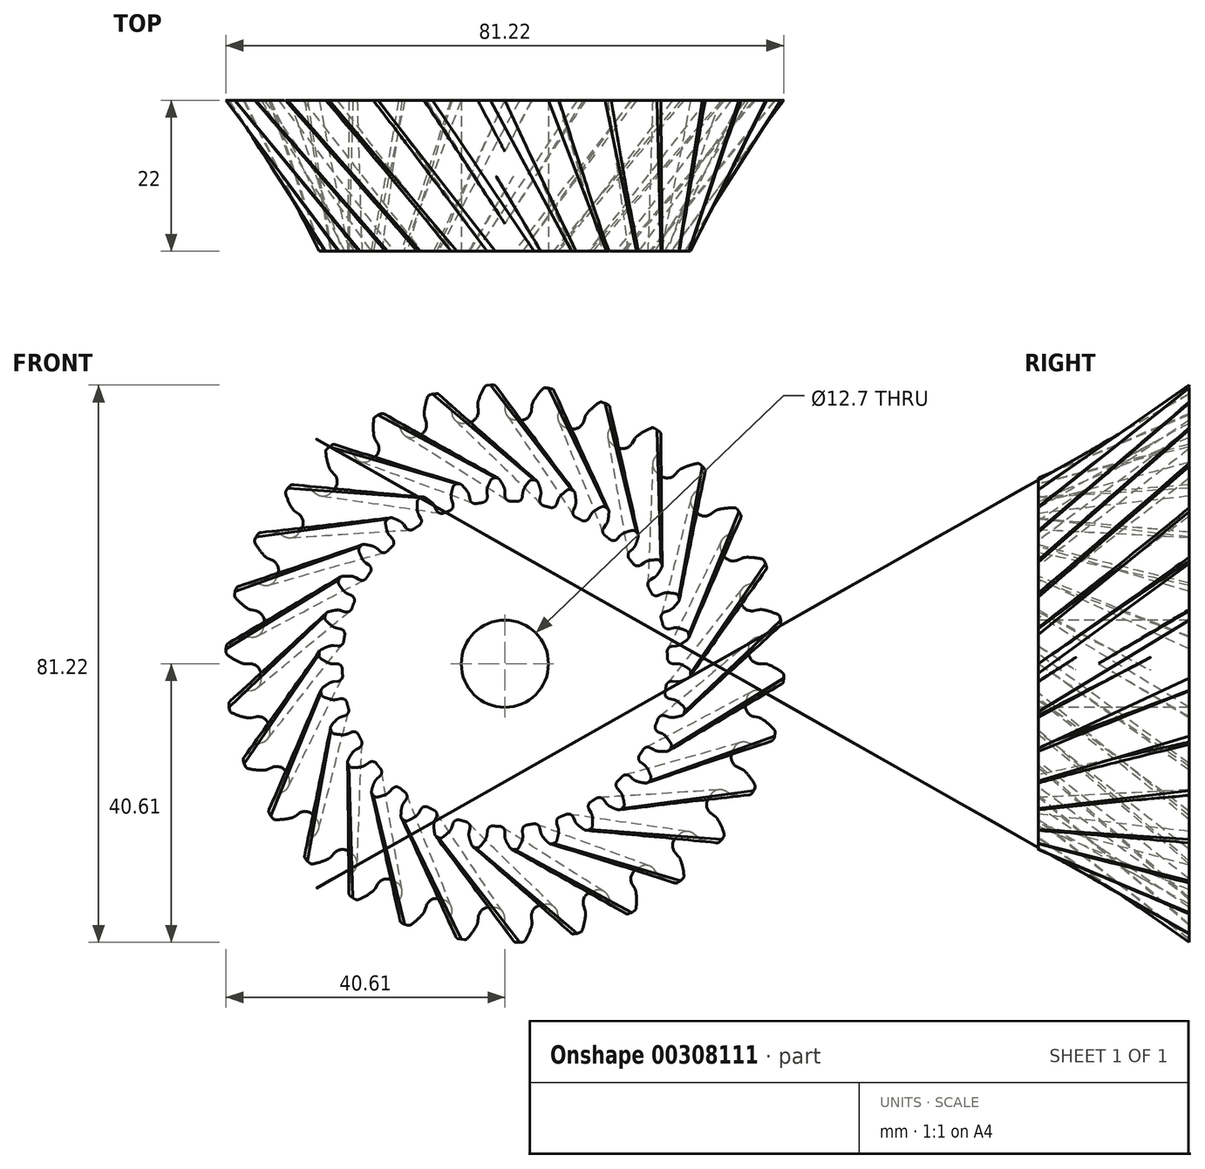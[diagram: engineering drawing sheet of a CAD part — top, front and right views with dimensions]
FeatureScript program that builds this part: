
annotation { "Feature Type Name" : "Feature", "Feature Type Description" : "" }
export const myFeature = defineFeature(function(context is Context, id is Id, definition is map)
    precondition{}
    {
        {
            var Q0;
            Q0=qCreatedBy(makeId("Front.planeOp"),FACE);
            var sketch = newSketch(context, id + "F0", { "sketchPlane" : qUnion([Q0])});
            skArc(sketch, "E0", {"start": v(-5.23, 35.17) * mm, "mid": v(-5.56, 35.12) * mm, "end": v(-5.9, 35.07) * mm});
            skArc(sketch, "E1.trimOffspring", {"start": v(-0.12, 38.41) * mm, "mid": v(-0.63, 39.45) * mm, "end": v(-1.27, 40.41) * mm});
            skLineSegment(sketch, "E2", {"start": v(-1.68, 40.61) * mm, "end": v(-2.13, 40.61) * mm});
            skLineSegment(sketch, "E3", {"start": v(0, 37.8) * mm, "end": v(0, 37.11) * mm});
            skLineSegment(sketch, "E4.MirrorCS", {"start": v(-2.58, 40.57) * mm, "end": v(-2.13, 40.61) * mm});
            skArc(sketch, "E5.MirrorCS", {"start": v(-3.9, 38.22) * mm, "mid": v(-3.5, 39.3) * mm, "end": v(-2.96, 40.32) * mm});
            skLineSegment(sketch, "E6.MirrorCS", {"start": v(-3.96, 37.58) * mm, "end": v(-3.89, 36.9) * mm});
            skPoint(sketch, "E7.visualSharp", {"position": v(-2.82, 40.54) * mm});
            skArc(sketch, "E7.filletArc", {"start": v(-2.58, 40.57) * mm, "mid": v(-2.8, 40.5) * mm, "end": v(-2.96, 40.32) * mm});
            skPoint(sketch, "E8.visualSharp", {"position": v(-1.43, 40.61) * mm});
            skArc(sketch, "E8.filletArc", {"start": v(-1.27, 40.41) * mm, "mid": v(-1.45, 40.56) * mm, "end": v(-1.68, 40.61) * mm});
            skPoint(sketch, "E9.visualSharp", {"position": v(-4, 37.9) * mm});
            skArc(sketch, "E9.filletArc", {"start": v(-3.9, 38.22) * mm, "mid": v(-3.96, 37.9) * mm, "end": v(-3.96, 37.58) * mm});
            skPoint(sketch, "E10.visualSharp", {"position": v(0, 38.1) * mm});
            skArc(sketch, "E10.filletArc", {"start": v(0, 37.8) * mm, "mid": v(-0.02, 38.1) * mm, "end": v(-0.12, 38.41) * mm});
            skPoint(sketch, "E11.visualSharp", {"position": v(0, 35.56) * mm});
            skArc(sketch, "E11.filletArc", {"start": v(0, 37.11) * mm, "mid": v(0.45, 36.02) * mm, "end": v(1.53, 35.53) * mm});
            skPoint(sketch, "E12.visualSharp", {"position": v(-3.73, 35.36) * mm});
            skArc(sketch, "E12.filletArc", {"start": v(-5.23, 35.17) * mm, "mid": v(-4.21, 35.77) * mm, "end": v(-3.89, 36.9) * mm});
            skArc(sketch, "E13.1.0", {"start": v(-12.43, 33.32) * mm, "mid": v(-11.56, 34.11) * mm, "end": v(-11.48, 35.3) * mm});
            skLineSegment(sketch, "E13.1.1", {"start": v(-11.69, 35.94) * mm, "end": v(-11.48, 35.3) * mm});
            skArc(sketch, "E13.1.2", {"start": v(-11.76, 36.57) * mm, "mid": v(-11.75, 36.25) * mm, "end": v(-11.69, 35.94) * mm});
            skArc(sketch, "E13.1.3", {"start": v(-11.76, 36.57) * mm, "mid": v(-11.59, 37.71) * mm, "end": v(-11.28, 38.83) * mm});
            skArc(sketch, "E13.1.4", {"start": v(-10.95, 39.15) * mm, "mid": v(-11.15, 39.02) * mm, "end": v(-11.28, 38.83) * mm});
            skLineSegment(sketch, "E13.1.5", {"start": v(-10.95, 39.15) * mm, "end": v(-10.53, 39.28) * mm});
            skLineSegment(sketch, "E13.1.6", {"start": v(-10.09, 39.38) * mm, "end": v(-10.53, 39.28) * mm});
            skArc(sketch, "E13.1.7", {"start": v(-9.65, 39.26) * mm, "mid": v(-9.85, 39.37) * mm, "end": v(-10.09, 39.38) * mm});
            skArc(sketch, "E13.1.8", {"start": v(-7.85, 36.97) * mm, "mid": v(-7.95, 37.27) * mm, "end": v(-8.1, 37.55) * mm});
            skLineSegment(sketch, "E13.1.9", {"start": v(-7.85, 36.97) * mm, "end": v(-7.7, 36.3) * mm});
            skArc(sketch, "E13.1.10", {"start": v(-7.7, 36.3) * mm, "mid": v(-7.05, 35.32) * mm, "end": v(-5.9, 35.07) * mm});
            skArc(sketch, "E13.1.11", {"start": v(-8.1, 37.55) * mm, "mid": v(-8.82, 38.45) * mm, "end": v(-9.65, 39.26) * mm});
            skArc(sketch, "E13.2.0", {"start": v(-19.09, 30) * mm, "mid": v(-18.4, 30.97) * mm, "end": v(-18.56, 32.14) * mm});
            skLineSegment(sketch, "E13.2.1", {"start": v(-18.9, 32.72) * mm, "end": v(-18.56, 32.14) * mm});
            skArc(sketch, "E13.2.2", {"start": v(-19.1, 33.33) * mm, "mid": v(-19.03, 33.01) * mm, "end": v(-18.9, 32.72) * mm});
            skArc(sketch, "E13.2.3", {"start": v(-19.1, 33.33) * mm, "mid": v(-19.17, 34.48) * mm, "end": v(-19.1, 35.63) * mm});
            skArc(sketch, "E13.2.4", {"start": v(-18.85, 36.01) * mm, "mid": v(-19.02, 35.85) * mm, "end": v(-19.1, 35.63) * mm});
            skLineSegment(sketch, "E13.2.5", {"start": v(-18.85, 36.01) * mm, "end": v(-18.46, 36.24) * mm});
            skLineSegment(sketch, "E13.2.6", {"start": v(-18.05, 36.42) * mm, "end": v(-18.46, 36.24) * mm});
            skArc(sketch, "E13.2.7", {"start": v(-17.6, 36.4) * mm, "mid": v(-17.82, 36.46) * mm, "end": v(-18.05, 36.42) * mm});
            skArc(sketch, "E13.2.8", {"start": v(-15.36, 34.53) * mm, "mid": v(-15.52, 34.8) * mm, "end": v(-15.73, 35.04) * mm});
            skLineSegment(sketch, "E13.2.9", {"start": v(-15.36, 34.53) * mm, "end": v(-15.09, 33.9) * mm});
            skArc(sketch, "E13.2.10", {"start": v(-15.09, 33.9) * mm, "mid": v(-14.24, 33.08) * mm, "end": v(-13.05, 33.08) * mm});
            skArc(sketch, "E13.2.11", {"start": v(-15.73, 35.04) * mm, "mid": v(-16.62, 35.78) * mm, "end": v(-17.6, 36.4) * mm});
            skArc(sketch, "E13.3.0", {"start": v(-24.9, 25.38) * mm, "mid": v(-24.43, 26.46) * mm, "end": v(-24.84, 27.57) * mm});
            skLineSegment(sketch, "E13.3.1", {"start": v(-25.3, 28.08) * mm, "end": v(-24.84, 27.57) * mm});
            skArc(sketch, "E13.3.2", {"start": v(-25.62, 28.63) * mm, "mid": v(-25.48, 28.34) * mm, "end": v(-25.3, 28.08) * mm});
            skArc(sketch, "E13.3.3", {"start": v(-25.62, 28.63) * mm, "mid": v(-25.92, 29.74) * mm, "end": v(-26.1, 30.88) * mm});
            skArc(sketch, "E13.3.4", {"start": v(-25.93, 31.3) * mm, "mid": v(-26.06, 31.11) * mm, "end": v(-26.1, 30.88) * mm});
            skLineSegment(sketch, "E13.3.5", {"start": v(-25.93, 31.3) * mm, "end": v(-25.6, 31.6) * mm});
            skLineSegment(sketch, "E13.3.6", {"start": v(-25.23, 31.87) * mm, "end": v(-25.6, 31.6) * mm});
            skArc(sketch, "E13.3.7", {"start": v(-24.78, 31.95) * mm, "mid": v(-25.02, 31.96) * mm, "end": v(-25.23, 31.87) * mm});
            skArc(sketch, "E13.3.8", {"start": v(-22.2, 30.58) * mm, "mid": v(-22.42, 30.82) * mm, "end": v(-22.67, 31) * mm});
            skLineSegment(sketch, "E13.3.9", {"start": v(-22.2, 30.58) * mm, "end": v(-21.8, 30.03) * mm});
            skArc(sketch, "E13.3.10", {"start": v(-21.8, 30.03) * mm, "mid": v(-20.8, 29.4) * mm, "end": v(-19.65, 29.64) * mm});
            skArc(sketch, "E13.3.11", {"start": v(-22.67, 31) * mm, "mid": v(-23.7, 31.54) * mm, "end": v(-24.78, 31.95) * mm});
            skArc(sketch, "E13.4.0", {"start": v(-29.64, 19.65) * mm, "mid": v(-29.4, 20.8) * mm, "end": v(-30.03, 21.8) * mm});
            skLineSegment(sketch, "E13.4.1", {"start": v(-30.58, 22.2) * mm, "end": v(-30.03, 21.8) * mm});
            skArc(sketch, "E13.4.2", {"start": v(-31, 22.67) * mm, "mid": v(-30.82, 22.42) * mm, "end": v(-30.58, 22.2) * mm});
            skArc(sketch, "E13.4.3", {"start": v(-31, 22.67) * mm, "mid": v(-31.54, 23.7) * mm, "end": v(-31.95, 24.78) * mm});
            skArc(sketch, "E13.4.4", {"start": v(-31.87, 25.23) * mm, "mid": v(-31.96, 25.02) * mm, "end": v(-31.95, 24.78) * mm});
            skLineSegment(sketch, "E13.4.5", {"start": v(-31.87, 25.23) * mm, "end": v(-31.6, 25.6) * mm});
            skLineSegment(sketch, "E13.4.6", {"start": v(-31.3, 25.93) * mm, "end": v(-31.6, 25.6) * mm});
            skArc(sketch, "E13.4.7", {"start": v(-30.88, 26.1) * mm, "mid": v(-31.11, 26.06) * mm, "end": v(-31.3, 25.93) * mm});
            skArc(sketch, "E13.4.8", {"start": v(-28.08, 25.3) * mm, "mid": v(-28.34, 25.48) * mm, "end": v(-28.63, 25.62) * mm});
            skLineSegment(sketch, "E13.4.9", {"start": v(-28.08, 25.3) * mm, "end": v(-27.57, 24.84) * mm});
            skArc(sketch, "E13.4.10", {"start": v(-27.57, 24.84) * mm, "mid": v(-26.46, 24.43) * mm, "end": v(-25.38, 24.9) * mm});
            skArc(sketch, "E13.4.11", {"start": v(-28.63, 25.62) * mm, "mid": v(-29.74, 25.92) * mm, "end": v(-30.88, 26.1) * mm});
            skArc(sketch, "E13.5.0", {"start": v(-33.08, 13.05) * mm, "mid": v(-33.08, 14.24) * mm, "end": v(-33.9, 15.09) * mm});
            skLineSegment(sketch, "E13.5.1", {"start": v(-34.53, 15.36) * mm, "end": v(-33.9, 15.09) * mm});
            skArc(sketch, "E13.5.2", {"start": v(-35.04, 15.73) * mm, "mid": v(-34.8, 15.52) * mm, "end": v(-34.53, 15.36) * mm});
            skArc(sketch, "E13.5.3", {"start": v(-35.04, 15.73) * mm, "mid": v(-35.78, 16.62) * mm, "end": v(-36.4, 17.6) * mm});
            skArc(sketch, "E13.5.4", {"start": v(-36.42, 18.05) * mm, "mid": v(-36.46, 17.82) * mm, "end": v(-36.4, 17.6) * mm});
            skLineSegment(sketch, "E13.5.5", {"start": v(-36.42, 18.05) * mm, "end": v(-36.24, 18.46) * mm});
            skLineSegment(sketch, "E13.5.6", {"start": v(-36.01, 18.85) * mm, "end": v(-36.24, 18.46) * mm});
            skArc(sketch, "E13.5.7", {"start": v(-35.63, 19.1) * mm, "mid": v(-35.85, 19.02) * mm, "end": v(-36.01, 18.85) * mm});
            skArc(sketch, "E13.5.8", {"start": v(-32.72, 18.9) * mm, "mid": v(-33.01, 19.03) * mm, "end": v(-33.33, 19.1) * mm});
            skLineSegment(sketch, "E13.5.9", {"start": v(-32.72, 18.9) * mm, "end": v(-32.14, 18.56) * mm});
            skArc(sketch, "E13.5.10", {"start": v(-32.14, 18.56) * mm, "mid": v(-30.97, 18.4) * mm, "end": v(-30, 19.09) * mm});
            skArc(sketch, "E13.5.11", {"start": v(-33.33, 19.1) * mm, "mid": v(-34.48, 19.17) * mm, "end": v(-35.63, 19.1) * mm});
            skArc(sketch, "E13.6.0", {"start": v(-35.07, 5.9) * mm, "mid": v(-35.32, 7.05) * mm, "end": v(-36.3, 7.7) * mm});
            skLineSegment(sketch, "E13.6.1", {"start": v(-36.97, 7.85) * mm, "end": v(-36.3, 7.7) * mm});
            skArc(sketch, "E13.6.2", {"start": v(-37.55, 8.1) * mm, "mid": v(-37.27, 7.95) * mm, "end": v(-36.97, 7.85) * mm});
            skArc(sketch, "E13.6.3", {"start": v(-37.55, 8.1) * mm, "mid": v(-38.45, 8.82) * mm, "end": v(-39.26, 9.65) * mm});
            skArc(sketch, "E13.6.4", {"start": v(-39.38, 10.09) * mm, "mid": v(-39.37, 9.85) * mm, "end": v(-39.26, 9.65) * mm});
            skLineSegment(sketch, "E13.6.5", {"start": v(-39.38, 10.09) * mm, "end": v(-39.28, 10.53) * mm});
            skLineSegment(sketch, "E13.6.6", {"start": v(-39.15, 10.95) * mm, "end": v(-39.28, 10.53) * mm});
            skArc(sketch, "E13.6.7", {"start": v(-38.83, 11.28) * mm, "mid": v(-39.02, 11.15) * mm, "end": v(-39.15, 10.95) * mm});
            skArc(sketch, "E13.6.8", {"start": v(-35.94, 11.69) * mm, "mid": v(-36.25, 11.75) * mm, "end": v(-36.57, 11.76) * mm});
            skLineSegment(sketch, "E13.6.9", {"start": v(-35.94, 11.69) * mm, "end": v(-35.3, 11.48) * mm});
            skArc(sketch, "E13.6.10", {"start": v(-35.3, 11.48) * mm, "mid": v(-34.11, 11.56) * mm, "end": v(-33.32, 12.43) * mm});
            skArc(sketch, "E13.6.11", {"start": v(-36.57, 11.76) * mm, "mid": v(-37.71, 11.59) * mm, "end": v(-38.83, 11.28) * mm});
            skArc(sketch, "E13.7.0", {"start": v(-35.53, -1.53) * mm, "mid": v(-36.02, -0.45) * mm, "end": v(-37.11, 0) * mm});
            skLineSegment(sketch, "E13.7.1", {"start": v(-37.8, 0) * mm, "end": v(-37.11, 0) * mm});
            skArc(sketch, "E13.7.2", {"start": v(-38.41, 0.12) * mm, "mid": v(-38.1, 0.02) * mm, "end": v(-37.8, 0) * mm});
            skArc(sketch, "E13.7.3", {"start": v(-38.41, 0.12) * mm, "mid": v(-39.45, 0.63) * mm, "end": v(-40.41, 1.27) * mm});
            skArc(sketch, "E13.7.4", {"start": v(-40.61, 1.68) * mm, "mid": v(-40.56, 1.45) * mm, "end": v(-40.41, 1.27) * mm});
            skLineSegment(sketch, "E13.7.5", {"start": v(-40.61, 1.68) * mm, "end": v(-40.61, 2.13) * mm});
            skLineSegment(sketch, "E13.7.6", {"start": v(-40.57, 2.58) * mm, "end": v(-40.61, 2.13) * mm});
            skArc(sketch, "E13.7.7", {"start": v(-40.32, 2.96) * mm, "mid": v(-40.5, 2.8) * mm, "end": v(-40.57, 2.58) * mm});
            skArc(sketch, "E13.7.8", {"start": v(-37.58, 3.96) * mm, "mid": v(-37.9, 3.96) * mm, "end": v(-38.22, 3.9) * mm});
            skLineSegment(sketch, "E13.7.9", {"start": v(-37.58, 3.96) * mm, "end": v(-36.9, 3.89) * mm});
            skArc(sketch, "E13.7.10", {"start": v(-36.9, 3.89) * mm, "mid": v(-35.77, 4.21) * mm, "end": v(-35.17, 5.23) * mm});
            skArc(sketch, "E13.7.11", {"start": v(-38.22, 3.9) * mm, "mid": v(-39.3, 3.5) * mm, "end": v(-40.32, 2.96) * mm});
            skArc(sketch, "E13.8.0", {"start": v(-34.43, -8.88) * mm, "mid": v(-35.13, -7.93) * mm, "end": v(-36.3, -7.72) * mm});
            skLineSegment(sketch, "E13.8.1", {"start": v(-36.96, -7.87) * mm, "end": v(-36.3, -7.72) * mm});
            skArc(sketch, "E13.8.2", {"start": v(-37.6, -7.87) * mm, "mid": v(-37.28, -7.9) * mm, "end": v(-36.96, -7.87) * mm});
            skArc(sketch, "E13.8.3", {"start": v(-37.6, -7.87) * mm, "mid": v(-38.72, -7.58) * mm, "end": v(-39.8, -7.16) * mm});
            skArc(sketch, "E13.8.4", {"start": v(-40.08, -6.8) * mm, "mid": v(-39.98, -7.01) * mm, "end": v(-39.8, -7.16) * mm});
            skLineSegment(sketch, "E13.8.5", {"start": v(-40.08, -6.8) * mm, "end": v(-40.17, -6.36) * mm});
            skLineSegment(sketch, "E13.8.6", {"start": v(-40.22, -5.92) * mm, "end": v(-40.17, -6.36) * mm});
            skArc(sketch, "E13.8.7", {"start": v(-40.06, -5.5) * mm, "mid": v(-40.19, -5.68) * mm, "end": v(-40.22, -5.92) * mm});
            skArc(sketch, "E13.8.8", {"start": v(-37.59, -3.94) * mm, "mid": v(-37.9, -4) * mm, "end": v(-38.2, -4.13) * mm});
            skLineSegment(sketch, "E13.8.9", {"start": v(-37.59, -3.94) * mm, "end": v(-36.91, -3.87) * mm});
            skArc(sketch, "E13.8.10", {"start": v(-36.91, -3.87) * mm, "mid": v(-35.86, -3.32) * mm, "end": v(-35.5, -2.2) * mm});
            skArc(sketch, "E13.8.11", {"start": v(-38.2, -4.13) * mm, "mid": v(-39.17, -4.75) * mm, "end": v(-40.06, -5.5) * mm});
            skArc(sketch, "E13.9.0", {"start": v(-31.83, -15.85) * mm, "mid": v(-32.72, -15.06) * mm, "end": v(-33.9, -15.1) * mm});
            skLineSegment(sketch, "E13.9.1", {"start": v(-34.52, -15.38) * mm, "end": v(-33.9, -15.1) * mm});
            skArc(sketch, "E13.9.2", {"start": v(-35.14, -15.52) * mm, "mid": v(-34.82, -15.48) * mm, "end": v(-34.52, -15.38) * mm});
            skArc(sketch, "E13.9.3", {"start": v(-35.14, -15.52) * mm, "mid": v(-36.3, -15.46) * mm, "end": v(-37.44, -15.27) * mm});
            skArc(sketch, "E13.9.4", {"start": v(-37.79, -14.99) * mm, "mid": v(-37.65, -15.17) * mm, "end": v(-37.44, -15.27) * mm});
            skLineSegment(sketch, "E13.9.5", {"start": v(-37.79, -14.99) * mm, "end": v(-37.97, -14.58) * mm});
            skLineSegment(sketch, "E13.9.6", {"start": v(-38.1, -14.15) * mm, "end": v(-37.97, -14.58) * mm});
            skArc(sketch, "E13.9.7", {"start": v(-38.04, -13.7) * mm, "mid": v(-38.13, -13.92) * mm, "end": v(-38.1, -14.15) * mm});
            skArc(sketch, "E13.9.8", {"start": v(-35.94, -11.67) * mm, "mid": v(-36.24, -11.8) * mm, "end": v(-36.5, -11.98) * mm});
            skLineSegment(sketch, "E13.9.9", {"start": v(-35.94, -11.67) * mm, "end": v(-35.3, -11.46) * mm});
            skArc(sketch, "E13.9.10", {"start": v(-35.3, -11.46) * mm, "mid": v(-34.4, -10.7) * mm, "end": v(-34.26, -9.53) * mm});
            skArc(sketch, "E13.9.11", {"start": v(-36.5, -11.98) * mm, "mid": v(-37.32, -12.8) * mm, "end": v(-38.04, -13.7) * mm});
            skArc(sketch, "E13.10.0", {"start": v(-27.84, -22.12) * mm, "mid": v(-28.87, -21.53) * mm, "end": v(-30.02, -21.82) * mm});
            skLineSegment(sketch, "E13.10.1", {"start": v(-30.57, -22.22) * mm, "end": v(-30.02, -21.82) * mm});
            skArc(sketch, "E13.10.2", {"start": v(-31.15, -22.48) * mm, "mid": v(-30.84, -22.38) * mm, "end": v(-30.57, -22.22) * mm});
            skArc(sketch, "E13.10.3", {"start": v(-31.15, -22.48) * mm, "mid": v(-32.29, -22.67) * mm, "end": v(-33.44, -22.72) * mm});
            skArc(sketch, "E13.10.4", {"start": v(-33.85, -22.51) * mm, "mid": v(-33.67, -22.67) * mm, "end": v(-33.44, -22.72) * mm});
            skLineSegment(sketch, "E13.10.5", {"start": v(-33.85, -22.51) * mm, "end": v(-34.1, -22.15) * mm});
            skLineSegment(sketch, "E13.10.6", {"start": v(-34.33, -21.76) * mm, "end": v(-34.1, -22.15) * mm});
            skArc(sketch, "E13.10.7", {"start": v(-34.36, -21.3) * mm, "mid": v(-34.4, -21.54) * mm, "end": v(-34.33, -21.76) * mm});
            skArc(sketch, "E13.10.8", {"start": v(-32.73, -18.89) * mm, "mid": v(-33, -19.07) * mm, "end": v(-33.2, -19.3) * mm});
            skLineSegment(sketch, "E13.10.9", {"start": v(-32.73, -18.89) * mm, "end": v(-32.15, -18.55) * mm});
            skArc(sketch, "E13.10.10", {"start": v(-32.15, -18.55) * mm, "mid": v(-31.41, -17.62) * mm, "end": v(-31.53, -16.44) * mm});
            skArc(sketch, "E13.10.11", {"start": v(-33.2, -19.3) * mm, "mid": v(-33.85, -20.27) * mm, "end": v(-34.36, -21.3) * mm});
            skArc(sketch, "E13.11.0", {"start": v(-22.64, -27.42) * mm, "mid": v(-23.76, -27.07) * mm, "end": v(-24.83, -27.59) * mm});
            skLineSegment(sketch, "E13.11.1", {"start": v(-25.28, -28.1) * mm, "end": v(-24.83, -27.59) * mm});
            skArc(sketch, "E13.11.2", {"start": v(-25.8, -28.47) * mm, "mid": v(-25.52, -28.3) * mm, "end": v(-25.28, -28.1) * mm});
            skArc(sketch, "E13.11.3", {"start": v(-25.8, -28.47) * mm, "mid": v(-26.87, -28.9) * mm, "end": v(-27.99, -29.18) * mm});
            skArc(sketch, "E13.11.4", {"start": v(-28.42, -29.06) * mm, "mid": v(-28.22, -29.17) * mm, "end": v(-27.99, -29.18) * mm});
            skLineSegment(sketch, "E13.11.5", {"start": v(-28.42, -29.06) * mm, "end": v(-28.76, -28.76) * mm});
            skLineSegment(sketch, "E13.11.6", {"start": v(-29.06, -28.42) * mm, "end": v(-28.76, -28.76) * mm});
            skArc(sketch, "E13.11.7", {"start": v(-29.18, -27.99) * mm, "mid": v(-29.17, -28.22) * mm, "end": v(-29.06, -28.42) * mm});
            skArc(sketch, "E13.11.8", {"start": v(-28.1, -25.28) * mm, "mid": v(-28.3, -25.52) * mm, "end": v(-28.47, -25.8) * mm});
            skLineSegment(sketch, "E13.11.9", {"start": v(-28.1, -25.28) * mm, "end": v(-27.59, -24.83) * mm});
            skArc(sketch, "E13.11.10", {"start": v(-27.59, -24.83) * mm, "mid": v(-27.07, -23.76) * mm, "end": v(-27.42, -22.64) * mm});
            skArc(sketch, "E13.11.11", {"start": v(-28.47, -25.8) * mm, "mid": v(-28.9, -26.87) * mm, "end": v(-29.18, -27.99) * mm});
            skArc(sketch, "E13.12.0", {"start": v(-16.44, -31.53) * mm, "mid": v(-17.62, -31.41) * mm, "end": v(-18.55, -32.15) * mm});
            skLineSegment(sketch, "E13.12.1", {"start": v(-18.89, -32.73) * mm, "end": v(-18.55, -32.15) * mm});
            skArc(sketch, "E13.12.2", {"start": v(-19.3, -33.2) * mm, "mid": v(-19.07, -33) * mm, "end": v(-18.89, -32.73) * mm});
            skArc(sketch, "E13.12.3", {"start": v(-19.3, -33.2) * mm, "mid": v(-20.27, -33.85) * mm, "end": v(-21.3, -34.36) * mm});
            skArc(sketch, "E13.12.4", {"start": v(-21.76, -34.33) * mm, "mid": v(-21.54, -34.4) * mm, "end": v(-21.3, -34.36) * mm});
            skLineSegment(sketch, "E13.12.5", {"start": v(-21.76, -34.33) * mm, "end": v(-22.15, -34.1) * mm});
            skLineSegment(sketch, "E13.12.6", {"start": v(-22.51, -33.85) * mm, "end": v(-22.15, -34.1) * mm});
            skArc(sketch, "E13.12.7", {"start": v(-22.72, -33.44) * mm, "mid": v(-22.67, -33.67) * mm, "end": v(-22.51, -33.85) * mm});
            skArc(sketch, "E13.12.8", {"start": v(-22.22, -30.57) * mm, "mid": v(-22.38, -30.84) * mm, "end": v(-22.48, -31.15) * mm});
            skLineSegment(sketch, "E13.12.9", {"start": v(-22.22, -30.57) * mm, "end": v(-21.82, -30.02) * mm});
            skArc(sketch, "E13.12.10", {"start": v(-21.82, -30.02) * mm, "mid": v(-21.53, -28.87) * mm, "end": v(-22.12, -27.84) * mm});
            skArc(sketch, "E13.12.11", {"start": v(-22.48, -31.15) * mm, "mid": v(-22.67, -32.29) * mm, "end": v(-22.72, -33.44) * mm});
            skArc(sketch, "E13.13.0", {"start": v(-9.53, -34.26) * mm, "mid": v(-10.7, -34.4) * mm, "end": v(-11.46, -35.3) * mm});
            skLineSegment(sketch, "E13.13.1", {"start": v(-11.67, -35.94) * mm, "end": v(-11.46, -35.3) * mm});
            skArc(sketch, "E13.13.2", {"start": v(-11.98, -36.5) * mm, "mid": v(-11.8, -36.24) * mm, "end": v(-11.67, -35.94) * mm});
            skArc(sketch, "E13.13.3", {"start": v(-11.98, -36.5) * mm, "mid": v(-12.8, -37.32) * mm, "end": v(-13.7, -38.04) * mm});
            skArc(sketch, "E13.13.4", {"start": v(-14.15, -38.1) * mm, "mid": v(-13.92, -38.13) * mm, "end": v(-13.7, -38.04) * mm});
            skLineSegment(sketch, "E13.13.5", {"start": v(-14.15, -38.1) * mm, "end": v(-14.58, -37.97) * mm});
            skLineSegment(sketch, "E13.13.6", {"start": v(-14.99, -37.79) * mm, "end": v(-14.58, -37.97) * mm});
            skArc(sketch, "E13.13.7", {"start": v(-15.27, -37.44) * mm, "mid": v(-15.17, -37.65) * mm, "end": v(-14.99, -37.79) * mm});
            skArc(sketch, "E13.13.8", {"start": v(-15.38, -34.52) * mm, "mid": v(-15.48, -34.82) * mm, "end": v(-15.52, -35.14) * mm});
            skLineSegment(sketch, "E13.13.9", {"start": v(-15.38, -34.52) * mm, "end": v(-15.1, -33.9) * mm});
            skArc(sketch, "E13.13.10", {"start": v(-15.1, -33.9) * mm, "mid": v(-15.06, -32.72) * mm, "end": v(-15.85, -31.83) * mm});
            skArc(sketch, "E13.13.11", {"start": v(-15.52, -35.14) * mm, "mid": v(-15.46, -36.3) * mm, "end": v(-15.27, -37.44) * mm});
            skArc(sketch, "E13.14.0", {"start": v(-2.2, -35.5) * mm, "mid": v(-3.32, -35.86) * mm, "end": v(-3.87, -36.91) * mm});
            skLineSegment(sketch, "E13.14.1", {"start": v(-3.94, -37.59) * mm, "end": v(-3.87, -36.91) * mm});
            skArc(sketch, "E13.14.2", {"start": v(-4.13, -38.2) * mm, "mid": v(-4, -37.9) * mm, "end": v(-3.94, -37.59) * mm});
            skArc(sketch, "E13.14.3", {"start": v(-4.13, -38.2) * mm, "mid": v(-4.75, -39.17) * mm, "end": v(-5.5, -40.06) * mm});
            skArc(sketch, "E13.14.4", {"start": v(-5.92, -40.22) * mm, "mid": v(-5.68, -40.19) * mm, "end": v(-5.5, -40.06) * mm});
            skLineSegment(sketch, "E13.14.5", {"start": v(-5.92, -40.22) * mm, "end": v(-6.36, -40.17) * mm});
            skLineSegment(sketch, "E13.14.6", {"start": v(-6.8, -40.08) * mm, "end": v(-6.36, -40.17) * mm});
            skArc(sketch, "E13.14.7", {"start": v(-7.16, -39.8) * mm, "mid": v(-7.01, -39.98) * mm, "end": v(-6.8, -40.08) * mm});
            skArc(sketch, "E13.14.8", {"start": v(-7.87, -36.96) * mm, "mid": v(-7.9, -37.28) * mm, "end": v(-7.87, -37.6) * mm});
            skLineSegment(sketch, "E13.14.9", {"start": v(-7.87, -36.96) * mm, "end": v(-7.72, -36.3) * mm});
            skArc(sketch, "E13.14.10", {"start": v(-7.72, -36.3) * mm, "mid": v(-7.93, -35.13) * mm, "end": v(-8.88, -34.43) * mm});
            skArc(sketch, "E13.14.11", {"start": v(-7.87, -37.6) * mm, "mid": v(-7.58, -38.72) * mm, "end": v(-7.16, -39.8) * mm});
            skArc(sketch, "E13.15.0", {"start": v(5.23, -35.17) * mm, "mid": v(4.21, -35.77) * mm, "end": v(3.89, -36.9) * mm});
            skLineSegment(sketch, "E13.15.1", {"start": v(3.96, -37.58) * mm, "end": v(3.89, -36.9) * mm});
            skArc(sketch, "E13.15.2", {"start": v(3.9, -38.22) * mm, "mid": v(3.96, -37.9) * mm, "end": v(3.96, -37.58) * mm});
            skArc(sketch, "E13.15.3", {"start": v(3.9, -38.22) * mm, "mid": v(3.5, -39.3) * mm, "end": v(2.96, -40.32) * mm});
            skArc(sketch, "E13.15.4", {"start": v(2.58, -40.57) * mm, "mid": v(2.8, -40.5) * mm, "end": v(2.96, -40.32) * mm});
            skLineSegment(sketch, "E13.15.5", {"start": v(2.58, -40.57) * mm, "end": v(2.13, -40.61) * mm});
            skLineSegment(sketch, "E13.15.6", {"start": v(1.68, -40.61) * mm, "end": v(2.13, -40.61) * mm});
            skArc(sketch, "E13.15.7", {"start": v(1.27, -40.41) * mm, "mid": v(1.45, -40.56) * mm, "end": v(1.68, -40.61) * mm});
            skArc(sketch, "E13.15.8", {"start": v(0, -37.8) * mm, "mid": v(0.02, -38.1) * mm, "end": v(0.12, -38.41) * mm});
            skLineSegment(sketch, "E13.15.9", {"start": v(0, -37.8) * mm, "end": v(0, -37.11) * mm});
            skArc(sketch, "E13.15.10", {"start": v(0, -37.11) * mm, "mid": v(-0.45, -36.02) * mm, "end": v(-1.53, -35.53) * mm});
            skArc(sketch, "E13.15.11", {"start": v(0.12, -38.41) * mm, "mid": v(0.63, -39.45) * mm, "end": v(1.27, -40.41) * mm});
            skArc(sketch, "E13.16.0", {"start": v(12.43, -33.32) * mm, "mid": v(11.56, -34.11) * mm, "end": v(11.48, -35.3) * mm});
            skLineSegment(sketch, "E13.16.1", {"start": v(11.69, -35.94) * mm, "end": v(11.48, -35.3) * mm});
            skArc(sketch, "E13.16.2", {"start": v(11.76, -36.57) * mm, "mid": v(11.75, -36.25) * mm, "end": v(11.69, -35.94) * mm});
            skArc(sketch, "E13.16.3", {"start": v(11.76, -36.57) * mm, "mid": v(11.59, -37.71) * mm, "end": v(11.28, -38.83) * mm});
            skArc(sketch, "E13.16.4", {"start": v(10.95, -39.15) * mm, "mid": v(11.15, -39.02) * mm, "end": v(11.28, -38.83) * mm});
            skLineSegment(sketch, "E13.16.5", {"start": v(10.95, -39.15) * mm, "end": v(10.53, -39.28) * mm});
            skLineSegment(sketch, "E13.16.6", {"start": v(10.09, -39.38) * mm, "end": v(10.53, -39.28) * mm});
            skArc(sketch, "E13.16.7", {"start": v(9.65, -39.26) * mm, "mid": v(9.85, -39.37) * mm, "end": v(10.09, -39.38) * mm});
            skArc(sketch, "E13.16.8", {"start": v(7.85, -36.97) * mm, "mid": v(7.95, -37.27) * mm, "end": v(8.1, -37.55) * mm});
            skLineSegment(sketch, "E13.16.9", {"start": v(7.85, -36.97) * mm, "end": v(7.7, -36.3) * mm});
            skArc(sketch, "E13.16.10", {"start": v(7.7, -36.3) * mm, "mid": v(7.05, -35.32) * mm, "end": v(5.9, -35.07) * mm});
            skArc(sketch, "E13.16.11", {"start": v(8.1, -37.55) * mm, "mid": v(8.82, -38.45) * mm, "end": v(9.65, -39.26) * mm});
            skArc(sketch, "E13.17.0", {"start": v(19.09, -30) * mm, "mid": v(18.4, -30.97) * mm, "end": v(18.56, -32.14) * mm});
            skLineSegment(sketch, "E13.17.1", {"start": v(18.9, -32.72) * mm, "end": v(18.56, -32.14) * mm});
            skArc(sketch, "E13.17.2", {"start": v(19.1, -33.33) * mm, "mid": v(19.03, -33.01) * mm, "end": v(18.9, -32.72) * mm});
            skArc(sketch, "E13.17.3", {"start": v(19.1, -33.33) * mm, "mid": v(19.17, -34.48) * mm, "end": v(19.1, -35.63) * mm});
            skArc(sketch, "E13.17.4", {"start": v(18.85, -36.01) * mm, "mid": v(19.02, -35.85) * mm, "end": v(19.1, -35.63) * mm});
            skLineSegment(sketch, "E13.17.5", {"start": v(18.85, -36.01) * mm, "end": v(18.46, -36.24) * mm});
            skLineSegment(sketch, "E13.17.6", {"start": v(18.05, -36.42) * mm, "end": v(18.46, -36.24) * mm});
            skArc(sketch, "E13.17.7", {"start": v(17.6, -36.4) * mm, "mid": v(17.82, -36.46) * mm, "end": v(18.05, -36.42) * mm});
            skArc(sketch, "E13.17.8", {"start": v(15.36, -34.53) * mm, "mid": v(15.52, -34.8) * mm, "end": v(15.73, -35.04) * mm});
            skLineSegment(sketch, "E13.17.9", {"start": v(15.36, -34.53) * mm, "end": v(15.09, -33.9) * mm});
            skArc(sketch, "E13.17.10", {"start": v(15.09, -33.9) * mm, "mid": v(14.24, -33.08) * mm, "end": v(13.05, -33.08) * mm});
            skArc(sketch, "E13.17.11", {"start": v(15.73, -35.04) * mm, "mid": v(16.62, -35.78) * mm, "end": v(17.6, -36.4) * mm});
            skArc(sketch, "E13.18.0", {"start": v(24.9, -25.38) * mm, "mid": v(24.43, -26.46) * mm, "end": v(24.84, -27.57) * mm});
            skLineSegment(sketch, "E13.18.1", {"start": v(25.3, -28.08) * mm, "end": v(24.84, -27.57) * mm});
            skArc(sketch, "E13.18.2", {"start": v(25.62, -28.63) * mm, "mid": v(25.48, -28.34) * mm, "end": v(25.3, -28.08) * mm});
            skArc(sketch, "E13.18.3", {"start": v(25.62, -28.63) * mm, "mid": v(25.92, -29.74) * mm, "end": v(26.1, -30.88) * mm});
            skArc(sketch, "E13.18.4", {"start": v(25.93, -31.3) * mm, "mid": v(26.06, -31.11) * mm, "end": v(26.1, -30.88) * mm});
            skLineSegment(sketch, "E13.18.5", {"start": v(25.93, -31.3) * mm, "end": v(25.6, -31.6) * mm});
            skLineSegment(sketch, "E13.18.6", {"start": v(25.23, -31.87) * mm, "end": v(25.6, -31.6) * mm});
            skArc(sketch, "E13.18.7", {"start": v(24.78, -31.95) * mm, "mid": v(25.02, -31.96) * mm, "end": v(25.23, -31.87) * mm});
            skArc(sketch, "E13.18.8", {"start": v(22.2, -30.58) * mm, "mid": v(22.42, -30.82) * mm, "end": v(22.67, -31) * mm});
            skLineSegment(sketch, "E13.18.9", {"start": v(22.2, -30.58) * mm, "end": v(21.8, -30.03) * mm});
            skArc(sketch, "E13.18.10", {"start": v(21.8, -30.03) * mm, "mid": v(20.8, -29.4) * mm, "end": v(19.65, -29.64) * mm});
            skArc(sketch, "E13.18.11", {"start": v(22.67, -31) * mm, "mid": v(23.7, -31.54) * mm, "end": v(24.78, -31.95) * mm});
            skArc(sketch, "E13.19.0", {"start": v(29.64, -19.65) * mm, "mid": v(29.4, -20.8) * mm, "end": v(30.03, -21.8) * mm});
            skLineSegment(sketch, "E13.19.1", {"start": v(30.58, -22.2) * mm, "end": v(30.03, -21.8) * mm});
            skArc(sketch, "E13.19.2", {"start": v(31, -22.67) * mm, "mid": v(30.82, -22.42) * mm, "end": v(30.58, -22.2) * mm});
            skArc(sketch, "E13.19.3", {"start": v(31, -22.67) * mm, "mid": v(31.54, -23.7) * mm, "end": v(31.95, -24.78) * mm});
            skArc(sketch, "E13.19.4", {"start": v(31.87, -25.23) * mm, "mid": v(31.96, -25.02) * mm, "end": v(31.95, -24.78) * mm});
            skLineSegment(sketch, "E13.19.5", {"start": v(31.87, -25.23) * mm, "end": v(31.6, -25.6) * mm});
            skLineSegment(sketch, "E13.19.6", {"start": v(31.3, -25.93) * mm, "end": v(31.6, -25.6) * mm});
            skArc(sketch, "E13.19.7", {"start": v(30.88, -26.1) * mm, "mid": v(31.11, -26.06) * mm, "end": v(31.3, -25.93) * mm});
            skArc(sketch, "E13.19.8", {"start": v(28.08, -25.3) * mm, "mid": v(28.34, -25.48) * mm, "end": v(28.63, -25.62) * mm});
            skLineSegment(sketch, "E13.19.9", {"start": v(28.08, -25.3) * mm, "end": v(27.57, -24.84) * mm});
            skArc(sketch, "E13.19.10", {"start": v(27.57, -24.84) * mm, "mid": v(26.46, -24.43) * mm, "end": v(25.38, -24.9) * mm});
            skArc(sketch, "E13.19.11", {"start": v(28.63, -25.62) * mm, "mid": v(29.74, -25.92) * mm, "end": v(30.88, -26.1) * mm});
            skArc(sketch, "E13.20.0", {"start": v(33.08, -13.05) * mm, "mid": v(33.08, -14.24) * mm, "end": v(33.9, -15.09) * mm});
            skLineSegment(sketch, "E13.20.1", {"start": v(34.53, -15.36) * mm, "end": v(33.9, -15.09) * mm});
            skArc(sketch, "E13.20.2", {"start": v(35.04, -15.73) * mm, "mid": v(34.8, -15.52) * mm, "end": v(34.53, -15.36) * mm});
            skArc(sketch, "E13.20.3", {"start": v(35.04, -15.73) * mm, "mid": v(35.78, -16.62) * mm, "end": v(36.4, -17.6) * mm});
            skArc(sketch, "E13.20.4", {"start": v(36.42, -18.05) * mm, "mid": v(36.46, -17.82) * mm, "end": v(36.4, -17.6) * mm});
            skLineSegment(sketch, "E13.20.5", {"start": v(36.42, -18.05) * mm, "end": v(36.24, -18.46) * mm});
            skLineSegment(sketch, "E13.20.6", {"start": v(36.01, -18.85) * mm, "end": v(36.24, -18.46) * mm});
            skArc(sketch, "E13.20.7", {"start": v(35.63, -19.1) * mm, "mid": v(35.85, -19.02) * mm, "end": v(36.01, -18.85) * mm});
            skArc(sketch, "E13.20.8", {"start": v(32.72, -18.9) * mm, "mid": v(33.01, -19.03) * mm, "end": v(33.33, -19.1) * mm});
            skLineSegment(sketch, "E13.20.9", {"start": v(32.72, -18.9) * mm, "end": v(32.14, -18.56) * mm});
            skArc(sketch, "E13.20.10", {"start": v(32.14, -18.56) * mm, "mid": v(30.97, -18.4) * mm, "end": v(30, -19.09) * mm});
            skArc(sketch, "E13.20.11", {"start": v(33.33, -19.1) * mm, "mid": v(34.48, -19.17) * mm, "end": v(35.63, -19.1) * mm});
            skArc(sketch, "E13.21.0", {"start": v(35.07, -5.9) * mm, "mid": v(35.32, -7.05) * mm, "end": v(36.3, -7.7) * mm});
            skLineSegment(sketch, "E13.21.1", {"start": v(36.97, -7.85) * mm, "end": v(36.3, -7.7) * mm});
            skArc(sketch, "E13.21.2", {"start": v(37.55, -8.1) * mm, "mid": v(37.27, -7.95) * mm, "end": v(36.97, -7.85) * mm});
            skArc(sketch, "E13.21.3", {"start": v(37.55, -8.1) * mm, "mid": v(38.45, -8.82) * mm, "end": v(39.26, -9.65) * mm});
            skArc(sketch, "E13.21.4", {"start": v(39.38, -10.09) * mm, "mid": v(39.37, -9.85) * mm, "end": v(39.26, -9.65) * mm});
            skLineSegment(sketch, "E13.21.5", {"start": v(39.38, -10.09) * mm, "end": v(39.28, -10.53) * mm});
            skLineSegment(sketch, "E13.21.6", {"start": v(39.15, -10.95) * mm, "end": v(39.28, -10.53) * mm});
            skArc(sketch, "E13.21.7", {"start": v(38.83, -11.28) * mm, "mid": v(39.02, -11.15) * mm, "end": v(39.15, -10.95) * mm});
            skArc(sketch, "E13.21.8", {"start": v(35.94, -11.69) * mm, "mid": v(36.25, -11.75) * mm, "end": v(36.57, -11.76) * mm});
            skLineSegment(sketch, "E13.21.9", {"start": v(35.94, -11.69) * mm, "end": v(35.3, -11.48) * mm});
            skArc(sketch, "E13.21.10", {"start": v(35.3, -11.48) * mm, "mid": v(34.11, -11.56) * mm, "end": v(33.32, -12.43) * mm});
            skArc(sketch, "E13.21.11", {"start": v(36.57, -11.76) * mm, "mid": v(37.71, -11.59) * mm, "end": v(38.83, -11.28) * mm});
            skArc(sketch, "E13.22.0", {"start": v(35.53, 1.53) * mm, "mid": v(36.02, 0.45) * mm, "end": v(37.11, 0) * mm});
            skLineSegment(sketch, "E13.22.1", {"start": v(37.8, 0) * mm, "end": v(37.11, 0) * mm});
            skArc(sketch, "E13.22.2", {"start": v(38.41, -0.12) * mm, "mid": v(38.1, -0.02) * mm, "end": v(37.8, 0) * mm});
            skArc(sketch, "E13.22.3", {"start": v(38.41, -0.12) * mm, "mid": v(39.45, -0.63) * mm, "end": v(40.41, -1.27) * mm});
            skArc(sketch, "E13.22.4", {"start": v(40.61, -1.68) * mm, "mid": v(40.56, -1.45) * mm, "end": v(40.41, -1.27) * mm});
            skLineSegment(sketch, "E13.22.5", {"start": v(40.61, -1.68) * mm, "end": v(40.61, -2.13) * mm});
            skLineSegment(sketch, "E13.22.6", {"start": v(40.57, -2.58) * mm, "end": v(40.61, -2.13) * mm});
            skArc(sketch, "E13.22.7", {"start": v(40.32, -2.96) * mm, "mid": v(40.5, -2.8) * mm, "end": v(40.57, -2.58) * mm});
            skArc(sketch, "E13.22.8", {"start": v(37.58, -3.96) * mm, "mid": v(37.9, -3.96) * mm, "end": v(38.22, -3.9) * mm});
            skLineSegment(sketch, "E13.22.9", {"start": v(37.58, -3.96) * mm, "end": v(36.9, -3.89) * mm});
            skArc(sketch, "E13.22.10", {"start": v(36.9, -3.89) * mm, "mid": v(35.77, -4.21) * mm, "end": v(35.17, -5.23) * mm});
            skArc(sketch, "E13.22.11", {"start": v(38.22, -3.9) * mm, "mid": v(39.3, -3.5) * mm, "end": v(40.32, -2.96) * mm});
            skArc(sketch, "E13.23.0", {"start": v(34.43, 8.88) * mm, "mid": v(35.13, 7.93) * mm, "end": v(36.3, 7.72) * mm});
            skLineSegment(sketch, "E13.23.1", {"start": v(36.96, 7.87) * mm, "end": v(36.3, 7.72) * mm});
            skArc(sketch, "E13.23.2", {"start": v(37.6, 7.87) * mm, "mid": v(37.28, 7.9) * mm, "end": v(36.96, 7.87) * mm});
            skArc(sketch, "E13.23.3", {"start": v(37.6, 7.87) * mm, "mid": v(38.72, 7.58) * mm, "end": v(39.8, 7.16) * mm});
            skArc(sketch, "E13.23.4", {"start": v(40.08, 6.8) * mm, "mid": v(39.98, 7.01) * mm, "end": v(39.8, 7.16) * mm});
            skLineSegment(sketch, "E13.23.5", {"start": v(40.08, 6.8) * mm, "end": v(40.17, 6.36) * mm});
            skLineSegment(sketch, "E13.23.6", {"start": v(40.22, 5.92) * mm, "end": v(40.17, 6.36) * mm});
            skArc(sketch, "E13.23.7", {"start": v(40.06, 5.5) * mm, "mid": v(40.19, 5.68) * mm, "end": v(40.22, 5.92) * mm});
            skArc(sketch, "E13.23.8", {"start": v(37.59, 3.94) * mm, "mid": v(37.9, 4) * mm, "end": v(38.2, 4.13) * mm});
            skLineSegment(sketch, "E13.23.9", {"start": v(37.59, 3.94) * mm, "end": v(36.91, 3.87) * mm});
            skArc(sketch, "E13.23.10", {"start": v(36.91, 3.87) * mm, "mid": v(35.86, 3.32) * mm, "end": v(35.5, 2.2) * mm});
            skArc(sketch, "E13.23.11", {"start": v(38.2, 4.13) * mm, "mid": v(39.17, 4.75) * mm, "end": v(40.06, 5.5) * mm});
            skArc(sketch, "E13.24.0", {"start": v(31.83, 15.85) * mm, "mid": v(32.72, 15.06) * mm, "end": v(33.9, 15.1) * mm});
            skLineSegment(sketch, "E13.24.1", {"start": v(34.52, 15.38) * mm, "end": v(33.9, 15.1) * mm});
            skArc(sketch, "E13.24.2", {"start": v(35.14, 15.52) * mm, "mid": v(34.82, 15.48) * mm, "end": v(34.52, 15.38) * mm});
            skArc(sketch, "E13.24.3", {"start": v(35.14, 15.52) * mm, "mid": v(36.3, 15.46) * mm, "end": v(37.44, 15.27) * mm});
            skArc(sketch, "E13.24.4", {"start": v(37.79, 14.99) * mm, "mid": v(37.65, 15.17) * mm, "end": v(37.44, 15.27) * mm});
            skLineSegment(sketch, "E13.24.5", {"start": v(37.79, 14.99) * mm, "end": v(37.97, 14.58) * mm});
            skLineSegment(sketch, "E13.24.6", {"start": v(38.1, 14.15) * mm, "end": v(37.97, 14.58) * mm});
            skArc(sketch, "E13.24.7", {"start": v(38.04, 13.7) * mm, "mid": v(38.13, 13.92) * mm, "end": v(38.1, 14.15) * mm});
            skArc(sketch, "E13.24.8", {"start": v(35.94, 11.67) * mm, "mid": v(36.24, 11.8) * mm, "end": v(36.5, 11.98) * mm});
            skLineSegment(sketch, "E13.24.9", {"start": v(35.94, 11.67) * mm, "end": v(35.3, 11.46) * mm});
            skArc(sketch, "E13.24.10", {"start": v(35.3, 11.46) * mm, "mid": v(34.4, 10.7) * mm, "end": v(34.26, 9.53) * mm});
            skArc(sketch, "E13.24.11", {"start": v(36.5, 11.98) * mm, "mid": v(37.32, 12.8) * mm, "end": v(38.04, 13.7) * mm});
            skArc(sketch, "E13.25.0", {"start": v(27.84, 22.12) * mm, "mid": v(28.87, 21.53) * mm, "end": v(30.02, 21.82) * mm});
            skLineSegment(sketch, "E13.25.1", {"start": v(30.57, 22.22) * mm, "end": v(30.02, 21.82) * mm});
            skArc(sketch, "E13.25.2", {"start": v(31.15, 22.48) * mm, "mid": v(30.84, 22.38) * mm, "end": v(30.57, 22.22) * mm});
            skArc(sketch, "E13.25.3", {"start": v(31.15, 22.48) * mm, "mid": v(32.29, 22.67) * mm, "end": v(33.44, 22.72) * mm});
            skArc(sketch, "E13.25.4", {"start": v(33.85, 22.51) * mm, "mid": v(33.67, 22.67) * mm, "end": v(33.44, 22.72) * mm});
            skLineSegment(sketch, "E13.25.5", {"start": v(33.85, 22.51) * mm, "end": v(34.1, 22.15) * mm});
            skLineSegment(sketch, "E13.25.6", {"start": v(34.33, 21.76) * mm, "end": v(34.1, 22.15) * mm});
            skArc(sketch, "E13.25.7", {"start": v(34.36, 21.3) * mm, "mid": v(34.4, 21.54) * mm, "end": v(34.33, 21.76) * mm});
            skArc(sketch, "E13.25.8", {"start": v(32.73, 18.89) * mm, "mid": v(33, 19.07) * mm, "end": v(33.2, 19.3) * mm});
            skLineSegment(sketch, "E13.25.9", {"start": v(32.73, 18.89) * mm, "end": v(32.15, 18.55) * mm});
            skArc(sketch, "E13.25.10", {"start": v(32.15, 18.55) * mm, "mid": v(31.41, 17.62) * mm, "end": v(31.53, 16.44) * mm});
            skArc(sketch, "E13.25.11", {"start": v(33.2, 19.3) * mm, "mid": v(33.85, 20.27) * mm, "end": v(34.36, 21.3) * mm});
            skArc(sketch, "E13.26.0", {"start": v(22.64, 27.42) * mm, "mid": v(23.76, 27.07) * mm, "end": v(24.83, 27.59) * mm});
            skLineSegment(sketch, "E13.26.1", {"start": v(25.28, 28.1) * mm, "end": v(24.83, 27.59) * mm});
            skArc(sketch, "E13.26.2", {"start": v(25.8, 28.47) * mm, "mid": v(25.52, 28.3) * mm, "end": v(25.28, 28.1) * mm});
            skArc(sketch, "E13.26.3", {"start": v(25.8, 28.47) * mm, "mid": v(26.87, 28.9) * mm, "end": v(27.99, 29.18) * mm});
            skArc(sketch, "E13.26.4", {"start": v(28.42, 29.06) * mm, "mid": v(28.22, 29.17) * mm, "end": v(27.99, 29.18) * mm});
            skLineSegment(sketch, "E13.26.5", {"start": v(28.42, 29.06) * mm, "end": v(28.76, 28.76) * mm});
            skLineSegment(sketch, "E13.26.6", {"start": v(29.06, 28.42) * mm, "end": v(28.76, 28.76) * mm});
            skArc(sketch, "E13.26.7", {"start": v(29.18, 27.99) * mm, "mid": v(29.17, 28.22) * mm, "end": v(29.06, 28.42) * mm});
            skArc(sketch, "E13.26.8", {"start": v(28.1, 25.28) * mm, "mid": v(28.3, 25.52) * mm, "end": v(28.47, 25.8) * mm});
            skLineSegment(sketch, "E13.26.9", {"start": v(28.1, 25.28) * mm, "end": v(27.59, 24.83) * mm});
            skArc(sketch, "E13.26.10", {"start": v(27.59, 24.83) * mm, "mid": v(27.07, 23.76) * mm, "end": v(27.42, 22.64) * mm});
            skArc(sketch, "E13.26.11", {"start": v(28.47, 25.8) * mm, "mid": v(28.9, 26.87) * mm, "end": v(29.18, 27.99) * mm});
            skArc(sketch, "E13.27.0", {"start": v(16.44, 31.53) * mm, "mid": v(17.62, 31.41) * mm, "end": v(18.55, 32.15) * mm});
            skLineSegment(sketch, "E13.27.1", {"start": v(18.89, 32.73) * mm, "end": v(18.55, 32.15) * mm});
            skArc(sketch, "E13.27.2", {"start": v(19.3, 33.2) * mm, "mid": v(19.07, 33) * mm, "end": v(18.89, 32.73) * mm});
            skArc(sketch, "E13.27.3", {"start": v(19.3, 33.2) * mm, "mid": v(20.27, 33.85) * mm, "end": v(21.3, 34.36) * mm});
            skArc(sketch, "E13.27.4", {"start": v(21.76, 34.33) * mm, "mid": v(21.54, 34.4) * mm, "end": v(21.3, 34.36) * mm});
            skLineSegment(sketch, "E13.27.5", {"start": v(21.76, 34.33) * mm, "end": v(22.15, 34.1) * mm});
            skLineSegment(sketch, "E13.27.6", {"start": v(22.51, 33.85) * mm, "end": v(22.15, 34.1) * mm});
            skArc(sketch, "E13.27.7", {"start": v(22.72, 33.44) * mm, "mid": v(22.67, 33.67) * mm, "end": v(22.51, 33.85) * mm});
            skArc(sketch, "E13.27.8", {"start": v(22.22, 30.57) * mm, "mid": v(22.38, 30.84) * mm, "end": v(22.48, 31.15) * mm});
            skLineSegment(sketch, "E13.27.9", {"start": v(22.22, 30.57) * mm, "end": v(21.82, 30.02) * mm});
            skArc(sketch, "E13.27.10", {"start": v(21.82, 30.02) * mm, "mid": v(21.53, 28.87) * mm, "end": v(22.12, 27.84) * mm});
            skArc(sketch, "E13.27.11", {"start": v(22.48, 31.15) * mm, "mid": v(22.67, 32.29) * mm, "end": v(22.72, 33.44) * mm});
            skArc(sketch, "E13.28.0", {"start": v(9.53, 34.26) * mm, "mid": v(10.7, 34.4) * mm, "end": v(11.46, 35.3) * mm});
            skLineSegment(sketch, "E13.28.1", {"start": v(11.67, 35.94) * mm, "end": v(11.46, 35.3) * mm});
            skArc(sketch, "E13.28.2", {"start": v(11.98, 36.5) * mm, "mid": v(11.8, 36.24) * mm, "end": v(11.67, 35.94) * mm});
            skArc(sketch, "E13.28.3", {"start": v(11.98, 36.5) * mm, "mid": v(12.8, 37.32) * mm, "end": v(13.7, 38.04) * mm});
            skArc(sketch, "E13.28.4", {"start": v(14.15, 38.1) * mm, "mid": v(13.92, 38.13) * mm, "end": v(13.7, 38.04) * mm});
            skLineSegment(sketch, "E13.28.5", {"start": v(14.15, 38.1) * mm, "end": v(14.58, 37.97) * mm});
            skLineSegment(sketch, "E13.28.6", {"start": v(14.99, 37.79) * mm, "end": v(14.58, 37.97) * mm});
            skArc(sketch, "E13.28.7", {"start": v(15.27, 37.44) * mm, "mid": v(15.17, 37.65) * mm, "end": v(14.99, 37.79) * mm});
            skArc(sketch, "E13.28.8", {"start": v(15.38, 34.52) * mm, "mid": v(15.48, 34.82) * mm, "end": v(15.52, 35.14) * mm});
            skLineSegment(sketch, "E13.28.9", {"start": v(15.38, 34.52) * mm, "end": v(15.1, 33.9) * mm});
            skArc(sketch, "E13.28.10", {"start": v(15.1, 33.9) * mm, "mid": v(15.06, 32.72) * mm, "end": v(15.85, 31.83) * mm});
            skArc(sketch, "E13.28.11", {"start": v(15.52, 35.14) * mm, "mid": v(15.46, 36.3) * mm, "end": v(15.27, 37.44) * mm});
            skArc(sketch, "E13.29.0", {"start": v(2.2, 35.5) * mm, "mid": v(3.32, 35.86) * mm, "end": v(3.87, 36.91) * mm});
            skLineSegment(sketch, "E13.29.1", {"start": v(3.94, 37.59) * mm, "end": v(3.87, 36.91) * mm});
            skArc(sketch, "E13.29.2", {"start": v(4.13, 38.2) * mm, "mid": v(4, 37.9) * mm, "end": v(3.94, 37.59) * mm});
            skArc(sketch, "E13.29.3", {"start": v(4.13, 38.2) * mm, "mid": v(4.75, 39.17) * mm, "end": v(5.5, 40.06) * mm});
            skArc(sketch, "E13.29.4", {"start": v(5.92, 40.22) * mm, "mid": v(5.68, 40.19) * mm, "end": v(5.5, 40.06) * mm});
            skLineSegment(sketch, "E13.29.5", {"start": v(5.92, 40.22) * mm, "end": v(6.36, 40.17) * mm});
            skLineSegment(sketch, "E13.29.6", {"start": v(6.8, 40.08) * mm, "end": v(6.36, 40.17) * mm});
            skArc(sketch, "E13.29.7", {"start": v(7.16, 39.8) * mm, "mid": v(7.01, 39.98) * mm, "end": v(6.8, 40.08) * mm});
            skArc(sketch, "E13.29.8", {"start": v(7.87, 36.96) * mm, "mid": v(7.9, 37.28) * mm, "end": v(7.87, 37.6) * mm});
            skLineSegment(sketch, "E13.29.9", {"start": v(7.87, 36.96) * mm, "end": v(7.72, 36.3) * mm});
            skArc(sketch, "E13.29.10", {"start": v(7.72, 36.3) * mm, "mid": v(7.93, 35.13) * mm, "end": v(8.88, 34.43) * mm});
            skArc(sketch, "E13.29.11", {"start": v(7.87, 37.6) * mm, "mid": v(7.58, 38.72) * mm, "end": v(7.16, 39.8) * mm});
            skArc(sketch, "E14.trimOffspring", {"start": v(2.2, 35.5) * mm, "mid": v(1.86, 35.51) * mm, "end": v(1.53, 35.53) * mm});
            skArc(sketch, "E15.trimOffspring", {"start": v(9.53, 34.26) * mm, "mid": v(9.2, 34.35) * mm, "end": v(8.88, 34.43) * mm});
            skArc(sketch, "E16.trimOffspring", {"start": v(16.44, 31.53) * mm, "mid": v(16.14, 31.68) * mm, "end": v(15.85, 31.83) * mm});
            skArc(sketch, "E17.trimOffspring", {"start": v(22.64, 27.42) * mm, "mid": v(22.38, 27.64) * mm, "end": v(22.12, 27.84) * mm});
            skArc(sketch, "E18.trimOffspring", {"start": v(27.84, 22.12) * mm, "mid": v(27.64, 22.38) * mm, "end": v(27.42, 22.64) * mm});
            skArc(sketch, "E19.trimOffspring", {"start": v(31.83, 15.85) * mm, "mid": v(31.68, 16.14) * mm, "end": v(31.53, 16.44) * mm});
            skArc(sketch, "E20.trimOffspring", {"start": v(34.43, 8.88) * mm, "mid": v(34.35, 9.2) * mm, "end": v(34.26, 9.53) * mm});
            skArc(sketch, "E21.trimOffspring", {"start": v(35.53, 1.53) * mm, "mid": v(35.51, 1.86) * mm, "end": v(35.5, 2.2) * mm});
            skArc(sketch, "E22.trimOffspring", {"start": v(35.07, -5.9) * mm, "mid": v(35.12, -5.56) * mm, "end": v(35.17, -5.23) * mm});
            skArc(sketch, "E23.trimOffspring", {"start": v(33.08, -13.05) * mm, "mid": v(33.2, -12.74) * mm, "end": v(33.32, -12.43) * mm});
            skArc(sketch, "E24.trimOffspring", {"start": v(29.64, -19.65) * mm, "mid": v(29.82, -19.37) * mm, "end": v(30, -19.09) * mm});
            skArc(sketch, "E25.trimOffspring", {"start": v(24.9, -25.38) * mm, "mid": v(25.14, -25.14) * mm, "end": v(25.38, -24.9) * mm});
            skArc(sketch, "E26.trimOffspring", {"start": v(-33.08, 13.05) * mm, "mid": v(-33.2, 12.74) * mm, "end": v(-33.32, 12.43) * mm});
            skArc(sketch, "E27.trimOffspring", {"start": v(-29.64, 19.65) * mm, "mid": v(-29.82, 19.37) * mm, "end": v(-30, 19.09) * mm});
            skArc(sketch, "E28.trimOffspring", {"start": v(-24.9, 25.38) * mm, "mid": v(-25.14, 25.14) * mm, "end": v(-25.38, 24.9) * mm});
            skArc(sketch, "E29.trimOffspring", {"start": v(-19.09, 30) * mm, "mid": v(-19.37, 29.82) * mm, "end": v(-19.65, 29.64) * mm});
            skArc(sketch, "E30.trimOffspring", {"start": v(-12.43, 33.32) * mm, "mid": v(-12.74, 33.2) * mm, "end": v(-13.05, 33.08) * mm});
            skArc(sketch, "E31.trimOffspring", {"start": v(-34.43, -8.88) * mm, "mid": v(-34.35, -9.2) * mm, "end": v(-34.26, -9.53) * mm});
            skArc(sketch, "E32.trimOffspring", {"start": v(-35.53, -1.53) * mm, "mid": v(-35.51, -1.86) * mm, "end": v(-35.5, -2.2) * mm});
            skArc(sketch, "E33.trimOffspring", {"start": v(-35.07, 5.9) * mm, "mid": v(-35.12, 5.56) * mm, "end": v(-35.17, 5.23) * mm});
            skArc(sketch, "E34.trimOffspring", {"start": v(-31.83, -15.85) * mm, "mid": v(-31.68, -16.14) * mm, "end": v(-31.53, -16.44) * mm});
            skArc(sketch, "E35.trimOffspring", {"start": v(-27.84, -22.12) * mm, "mid": v(-27.64, -22.38) * mm, "end": v(-27.42, -22.64) * mm});
            skArc(sketch, "E36.trimOffspring", {"start": v(-22.64, -27.42) * mm, "mid": v(-22.38, -27.64) * mm, "end": v(-22.12, -27.84) * mm});
            skArc(sketch, "E37.trimOffspring", {"start": v(-16.44, -31.53) * mm, "mid": v(-16.14, -31.68) * mm, "end": v(-15.85, -31.83) * mm});
            skArc(sketch, "E38.trimOffspring", {"start": v(-9.53, -34.26) * mm, "mid": v(-9.2, -34.35) * mm, "end": v(-8.88, -34.43) * mm});
            skArc(sketch, "E39.trimOffspring", {"start": v(-2.2, -35.5) * mm, "mid": v(-1.86, -35.51) * mm, "end": v(-1.53, -35.53) * mm});
            skArc(sketch, "E40.trimOffspring", {"start": v(5.23, -35.17) * mm, "mid": v(5.56, -35.12) * mm, "end": v(5.9, -35.07) * mm});
            skArc(sketch, "E41.trimOffspring", {"start": v(12.43, -33.32) * mm, "mid": v(12.74, -33.2) * mm, "end": v(13.05, -33.08) * mm});
            skArc(sketch, "E42.trimOffspring", {"start": v(19.09, -30) * mm, "mid": v(19.37, -29.82) * mm, "end": v(19.65, -29.64) * mm});
            skSolve(sketch);
        }
        {
            var Q0;
            Q0=makeQuery(id+"F0.imprint","IMPRINT",FACE,{"disambiguationData":[TD([[makeQuery(id+"F0.imprint","IMPRINT",EDGE,{"derivedFrom":sQuery(id+"F0.wireOp",EDGE,"E0")}),1.0]])]});
            cPlane(context, id + "F1", {"entities" : qUnion([Q0]), "cplaneType" : CPlaneType.OFFSET, "offset" : 22 * mm, "width" : 152.4 * mm, "height" : 152.4 * mm});
        }
        {
            var Q0;
            Q0=qCreatedBy(id+"F1.planeOp",FACE);
            var sketch = newSketch(context, id + "F2", { "sketchPlane" : qUnion([Q0])});
            skArc(sketch, "E43", {"start": v(-3.25, 23.48) * mm, "mid": v(-3.7, 23.41) * mm, "end": v(-4.17, 23.34) * mm});
            skArc(sketch, "E44.trimOffspring", {"start": v(-0.14, 25.74) * mm, "mid": v(-0.44, 26.32) * mm, "end": v(-0.8, 26.87) * mm});
            skLineSegment(sketch, "E45", {"start": v(0, 25.08) * mm, "end": v(0, 24.49) * mm});
            skLineSegment(sketch, "E46", {"start": v(-1.2, 27.08) * mm, "end": v(-1.42, 27.08) * mm});
            skLineSegment(sketch, "E47.MirrorCS", {"start": v(-1.63, 27.05) * mm, "end": v(-1.42, 27.08) * mm});
            skArc(sketch, "E48.MirrorCS", {"start": v(-2.56, 25.61) * mm, "mid": v(-2.32, 26.22) * mm, "end": v(-2.02, 26.8) * mm});
            skLineSegment(sketch, "E49.MirrorCS", {"start": v(-2.63, 24.95) * mm, "end": v(-2.57, 24.35) * mm});
            skPoint(sketch, "E50.visualSharp", {"position": v(-1.88, 27.03) * mm});
            skArc(sketch, "E50.filletArc", {"start": v(-1.63, 27.05) * mm, "mid": v(-1.86, 26.98) * mm, "end": v(-2.02, 26.8) * mm});
            skPoint(sketch, "E51.visualSharp", {"position": v(-0.95, 27.08) * mm});
            skArc(sketch, "E51.filletArc", {"start": v(-0.8, 26.87) * mm, "mid": v(-0.97, 27.02) * mm, "end": v(-1.2, 27.08) * mm});
            skPoint(sketch, "E52.visualSharp", {"position": v(-2.66, 25.26) * mm});
            skArc(sketch, "E52.filletArc", {"start": v(-2.56, 25.61) * mm, "mid": v(-2.63, 25.28) * mm, "end": v(-2.63, 24.95) * mm});
            skPoint(sketch, "E53.visualSharp", {"position": v(0, 25.4) * mm});
            skArc(sketch, "E53.filletArc", {"start": v(0, 25.08) * mm, "mid": v(-0.03, 25.42) * mm, "end": v(-0.14, 25.74) * mm});
            skPoint(sketch, "E54.visualSharp", {"position": v(-2.48, 23.58) * mm});
            skArc(sketch, "E54.filletArc", {"start": v(-3.25, 23.48) * mm, "mid": v(-2.73, 23.78) * mm, "end": v(-2.57, 24.35) * mm});
            skPoint(sketch, "E55.visualSharp", {"position": v(0, 23.7) * mm});
            skArc(sketch, "E55.filletArc", {"start": v(0, 24.49) * mm, "mid": v(0.23, 23.94) * mm, "end": v(0.77, 23.7) * mm});
            skArc(sketch, "E56.1.0", {"start": v(-8.06, 22.3) * mm, "mid": v(-7.61, 22.7) * mm, "end": v(-7.57, 23.29) * mm});
            skLineSegment(sketch, "E56.1.1", {"start": v(-7.76, 23.85) * mm, "end": v(-7.57, 23.29) * mm});
            skArc(sketch, "E56.1.2", {"start": v(-7.82, 24.52) * mm, "mid": v(-7.83, 24.18) * mm, "end": v(-7.76, 23.85) * mm});
            skArc(sketch, "E56.1.3", {"start": v(-7.82, 24.52) * mm, "mid": v(-7.72, 25.17) * mm, "end": v(-7.55, 25.8) * mm});
            skArc(sketch, "E56.1.4", {"start": v(-7.22, 26.12) * mm, "mid": v(-7.42, 26) * mm, "end": v(-7.55, 25.8) * mm});
            skLineSegment(sketch, "E56.1.5", {"start": v(-7.22, 26.12) * mm, "end": v(-7.02, 26.19) * mm});
            skLineSegment(sketch, "E56.1.6", {"start": v(-6.8, 26.23) * mm, "end": v(-7.02, 26.19) * mm});
            skArc(sketch, "E56.1.7", {"start": v(-6.36, 26.12) * mm, "mid": v(-6.57, 26.23) * mm, "end": v(-6.8, 26.23) * mm});
            skArc(sketch, "E56.1.8", {"start": v(-5.48, 25.15) * mm, "mid": v(-5.9, 25.65) * mm, "end": v(-6.36, 26.12) * mm});
            skArc(sketch, "E56.1.9", {"start": v(-5.2, 24.54) * mm, "mid": v(-5.31, 24.86) * mm, "end": v(-5.48, 25.15) * mm});
            skLineSegment(sketch, "E56.1.10", {"start": v(-5.2, 24.54) * mm, "end": v(-5.09, 23.95) * mm});
            skArc(sketch, "E56.1.11", {"start": v(-5.09, 23.95) * mm, "mid": v(-4.75, 23.46) * mm, "end": v(-4.17, 23.34) * mm});
            skArc(sketch, "E56.2.0", {"start": v(-12.52, 20.13) * mm, "mid": v(-12.17, 20.61) * mm, "end": v(-12.25, 21.2) * mm});
            skLineSegment(sketch, "E56.2.1", {"start": v(-12.55, 21.72) * mm, "end": v(-12.25, 21.2) * mm});
            skArc(sketch, "E56.2.2", {"start": v(-12.75, 22.36) * mm, "mid": v(-12.68, 22.03) * mm, "end": v(-12.55, 21.72) * mm});
            skArc(sketch, "E56.2.3", {"start": v(-12.75, 22.36) * mm, "mid": v(-12.78, 23.01) * mm, "end": v(-12.75, 23.67) * mm});
            skArc(sketch, "E56.2.4", {"start": v(-12.5, 24.05) * mm, "mid": v(-12.67, 23.89) * mm, "end": v(-12.75, 23.67) * mm});
            skLineSegment(sketch, "E56.2.5", {"start": v(-12.5, 24.05) * mm, "end": v(-12.3, 24.16) * mm});
            skLineSegment(sketch, "E56.2.6", {"start": v(-12.11, 24.25) * mm, "end": v(-12.3, 24.16) * mm});
            skArc(sketch, "E56.2.7", {"start": v(-11.65, 24.22) * mm, "mid": v(-11.88, 24.29) * mm, "end": v(-12.11, 24.25) * mm});
            skArc(sketch, "E56.2.8", {"start": v(-10.6, 23.46) * mm, "mid": v(-11.1, 23.87) * mm, "end": v(-11.65, 24.22) * mm});
            skArc(sketch, "E56.2.9", {"start": v(-10.2, 22.92) * mm, "mid": v(-10.37, 23.2) * mm, "end": v(-10.6, 23.46) * mm});
            skLineSegment(sketch, "E56.2.10", {"start": v(-10.2, 22.92) * mm, "end": v(-9.95, 22.37) * mm});
            skArc(sketch, "E56.2.11", {"start": v(-9.95, 22.37) * mm, "mid": v(-9.53, 21.96) * mm, "end": v(-8.93, 21.96) * mm});
            skArc(sketch, "E56.3.0", {"start": v(-16.43, 17.1) * mm, "mid": v(-16.19, 17.63) * mm, "end": v(-16.39, 18.2) * mm});
            skLineSegment(sketch, "E56.3.1", {"start": v(-16.79, 18.64) * mm, "end": v(-16.39, 18.2) * mm});
            skArc(sketch, "E56.3.2", {"start": v(-17.12, 19.22) * mm, "mid": v(-16.99, 18.9) * mm, "end": v(-16.79, 18.64) * mm});
            skArc(sketch, "E56.3.3", {"start": v(-17.12, 19.22) * mm, "mid": v(-17.29, 19.85) * mm, "end": v(-17.39, 20.5) * mm});
            skArc(sketch, "E56.3.4", {"start": v(-17.22, 20.93) * mm, "mid": v(-17.36, 20.73) * mm, "end": v(-17.39, 20.5) * mm});
            skLineSegment(sketch, "E56.3.5", {"start": v(-17.22, 20.93) * mm, "end": v(-17.06, 21.07) * mm});
            skLineSegment(sketch, "E56.3.6", {"start": v(-16.89, 21.2) * mm, "end": v(-17.06, 21.07) * mm});
            skArc(sketch, "E56.3.7", {"start": v(-16.44, 21.27) * mm, "mid": v(-16.67, 21.29) * mm, "end": v(-16.89, 21.2) * mm});
            skArc(sketch, "E56.3.8", {"start": v(-15.24, 20.74) * mm, "mid": v(-15.82, 21.04) * mm, "end": v(-16.44, 21.27) * mm});
            skArc(sketch, "E56.3.9", {"start": v(-14.74, 20.3) * mm, "mid": v(-14.96, 20.55) * mm, "end": v(-15.24, 20.74) * mm});
            skLineSegment(sketch, "E56.3.10", {"start": v(-14.74, 20.3) * mm, "end": v(-14.39, 19.81) * mm});
            skArc(sketch, "E56.3.11", {"start": v(-14.39, 19.81) * mm, "mid": v(-13.88, 19.5) * mm, "end": v(-13.3, 19.62) * mm});
            skArc(sketch, "E56.4.0", {"start": v(-19.62, 13.3) * mm, "mid": v(-19.5, 13.88) * mm, "end": v(-19.81, 14.39) * mm});
            skLineSegment(sketch, "E56.4.1", {"start": v(-20.3, 14.74) * mm, "end": v(-19.81, 14.39) * mm});
            skArc(sketch, "E56.4.2", {"start": v(-20.74, 15.24) * mm, "mid": v(-20.55, 14.96) * mm, "end": v(-20.3, 14.74) * mm});
            skArc(sketch, "E56.4.3", {"start": v(-20.74, 15.24) * mm, "mid": v(-21.04, 15.82) * mm, "end": v(-21.27, 16.44) * mm});
            skArc(sketch, "E56.4.4", {"start": v(-21.2, 16.89) * mm, "mid": v(-21.29, 16.67) * mm, "end": v(-21.27, 16.44) * mm});
            skLineSegment(sketch, "E56.4.5", {"start": v(-21.2, 16.89) * mm, "end": v(-21.07, 17.06) * mm});
            skLineSegment(sketch, "E56.4.6", {"start": v(-20.93, 17.22) * mm, "end": v(-21.07, 17.06) * mm});
            skArc(sketch, "E56.4.7", {"start": v(-20.5, 17.39) * mm, "mid": v(-20.73, 17.36) * mm, "end": v(-20.93, 17.22) * mm});
            skArc(sketch, "E56.4.8", {"start": v(-19.22, 17.12) * mm, "mid": v(-19.85, 17.29) * mm, "end": v(-20.5, 17.39) * mm});
            skArc(sketch, "E56.4.9", {"start": v(-18.64, 16.79) * mm, "mid": v(-18.9, 16.99) * mm, "end": v(-19.22, 17.12) * mm});
            skLineSegment(sketch, "E56.4.10", {"start": v(-18.64, 16.79) * mm, "end": v(-18.2, 16.39) * mm});
            skArc(sketch, "E56.4.11", {"start": v(-18.2, 16.39) * mm, "mid": v(-17.63, 16.19) * mm, "end": v(-17.1, 16.43) * mm});
            skArc(sketch, "E56.5.0", {"start": v(-21.96, 8.93) * mm, "mid": v(-21.96, 9.53) * mm, "end": v(-22.37, 9.95) * mm});
            skLineSegment(sketch, "E56.5.1", {"start": v(-22.92, 10.2) * mm, "end": v(-22.37, 9.95) * mm});
            skArc(sketch, "E56.5.2", {"start": v(-23.46, 10.6) * mm, "mid": v(-23.2, 10.37) * mm, "end": v(-22.92, 10.2) * mm});
            skArc(sketch, "E56.5.3", {"start": v(-23.46, 10.6) * mm, "mid": v(-23.87, 11.1) * mm, "end": v(-24.22, 11.65) * mm});
            skArc(sketch, "E56.5.4", {"start": v(-24.25, 12.11) * mm, "mid": v(-24.29, 11.88) * mm, "end": v(-24.22, 11.65) * mm});
            skLineSegment(sketch, "E56.5.5", {"start": v(-24.25, 12.11) * mm, "end": v(-24.16, 12.3) * mm});
            skLineSegment(sketch, "E56.5.6", {"start": v(-24.05, 12.5) * mm, "end": v(-24.16, 12.3) * mm});
            skArc(sketch, "E56.5.7", {"start": v(-23.67, 12.75) * mm, "mid": v(-23.89, 12.67) * mm, "end": v(-24.05, 12.5) * mm});
            skArc(sketch, "E56.5.8", {"start": v(-22.36, 12.75) * mm, "mid": v(-23.01, 12.78) * mm, "end": v(-23.67, 12.75) * mm});
            skArc(sketch, "E56.5.9", {"start": v(-21.72, 12.55) * mm, "mid": v(-22.03, 12.68) * mm, "end": v(-22.36, 12.75) * mm});
            skLineSegment(sketch, "E56.5.10", {"start": v(-21.72, 12.55) * mm, "end": v(-21.2, 12.25) * mm});
            skArc(sketch, "E56.5.11", {"start": v(-21.2, 12.25) * mm, "mid": v(-20.61, 12.17) * mm, "end": v(-20.13, 12.52) * mm});
            skArc(sketch, "E56.6.0", {"start": v(-23.34, 4.17) * mm, "mid": v(-23.46, 4.75) * mm, "end": v(-23.95, 5.09) * mm});
            skLineSegment(sketch, "E56.6.1", {"start": v(-24.54, 5.2) * mm, "end": v(-23.95, 5.09) * mm});
            skArc(sketch, "E56.6.2", {"start": v(-25.15, 5.48) * mm, "mid": v(-24.86, 5.31) * mm, "end": v(-24.54, 5.2) * mm});
            skArc(sketch, "E56.6.3", {"start": v(-25.15, 5.48) * mm, "mid": v(-25.65, 5.9) * mm, "end": v(-26.12, 6.36) * mm});
            skArc(sketch, "E56.6.4", {"start": v(-26.23, 6.8) * mm, "mid": v(-26.23, 6.57) * mm, "end": v(-26.12, 6.36) * mm});
            skLineSegment(sketch, "E56.6.5", {"start": v(-26.23, 6.8) * mm, "end": v(-26.19, 7.02) * mm});
            skLineSegment(sketch, "E56.6.6", {"start": v(-26.12, 7.22) * mm, "end": v(-26.19, 7.02) * mm});
            skArc(sketch, "E56.6.7", {"start": v(-25.8, 7.55) * mm, "mid": v(-26, 7.42) * mm, "end": v(-26.12, 7.22) * mm});
            skArc(sketch, "E56.6.8", {"start": v(-24.52, 7.82) * mm, "mid": v(-25.17, 7.72) * mm, "end": v(-25.8, 7.55) * mm});
            skArc(sketch, "E56.6.9", {"start": v(-23.85, 7.76) * mm, "mid": v(-24.18, 7.83) * mm, "end": v(-24.52, 7.82) * mm});
            skLineSegment(sketch, "E56.6.10", {"start": v(-23.85, 7.76) * mm, "end": v(-23.29, 7.57) * mm});
            skArc(sketch, "E56.6.11", {"start": v(-23.29, 7.57) * mm, "mid": v(-22.7, 7.61) * mm, "end": v(-22.3, 8.06) * mm});
            skArc(sketch, "E56.7.0", {"start": v(-23.7, -0.77) * mm, "mid": v(-23.94, -0.23) * mm, "end": v(-24.49, 0) * mm});
            skLineSegment(sketch, "E56.7.1", {"start": v(-25.08, 0) * mm, "end": v(-24.49, 0) * mm});
            skArc(sketch, "E56.7.2", {"start": v(-25.74, 0.14) * mm, "mid": v(-25.42, 0.03) * mm, "end": v(-25.08, 0) * mm});
            skArc(sketch, "E56.7.3", {"start": v(-25.74, 0.14) * mm, "mid": v(-26.32, 0.44) * mm, "end": v(-26.87, 0.8) * mm});
            skArc(sketch, "E56.7.4", {"start": v(-27.08, 1.2) * mm, "mid": v(-27.02, 0.97) * mm, "end": v(-26.87, 0.8) * mm});
            skLineSegment(sketch, "E56.7.5", {"start": v(-27.08, 1.2) * mm, "end": v(-27.08, 1.42) * mm});
            skLineSegment(sketch, "E56.7.6", {"start": v(-27.05, 1.63) * mm, "end": v(-27.08, 1.42) * mm});
            skArc(sketch, "E56.7.7", {"start": v(-26.8, 2.02) * mm, "mid": v(-26.98, 1.86) * mm, "end": v(-27.05, 1.63) * mm});
            skArc(sketch, "E56.7.8", {"start": v(-25.61, 2.56) * mm, "mid": v(-26.22, 2.32) * mm, "end": v(-26.8, 2.02) * mm});
            skArc(sketch, "E56.7.9", {"start": v(-24.95, 2.63) * mm, "mid": v(-25.28, 2.63) * mm, "end": v(-25.61, 2.56) * mm});
            skLineSegment(sketch, "E56.7.10", {"start": v(-24.95, 2.63) * mm, "end": v(-24.35, 2.57) * mm});
            skArc(sketch, "E56.7.11", {"start": v(-24.35, 2.57) * mm, "mid": v(-23.78, 2.73) * mm, "end": v(-23.48, 3.25) * mm});
            skArc(sketch, "E56.8.0", {"start": v(-23.02, -5.68) * mm, "mid": v(-23.36, -5.2) * mm, "end": v(-23.95, -5.1) * mm});
            skLineSegment(sketch, "E56.8.1", {"start": v(-24.53, -5.22) * mm, "end": v(-23.95, -5.1) * mm});
            skArc(sketch, "E56.8.2", {"start": v(-25.2, -5.22) * mm, "mid": v(-24.87, -5.26) * mm, "end": v(-24.53, -5.22) * mm});
            skArc(sketch, "E56.8.3", {"start": v(-25.2, -5.22) * mm, "mid": v(-25.84, -5.05) * mm, "end": v(-26.45, -4.8) * mm});
            skArc(sketch, "E56.8.4", {"start": v(-26.74, -4.45) * mm, "mid": v(-26.63, -4.66) * mm, "end": v(-26.45, -4.8) * mm});
            skLineSegment(sketch, "E56.8.5", {"start": v(-26.74, -4.45) * mm, "end": v(-26.78, -4.24) * mm});
            skLineSegment(sketch, "E56.8.6", {"start": v(-26.8, -4.03) * mm, "end": v(-26.78, -4.24) * mm});
            skArc(sketch, "E56.8.7", {"start": v(-26.64, -3.6) * mm, "mid": v(-26.77, -3.8) * mm, "end": v(-26.8, -4.03) * mm});
            skArc(sketch, "E56.8.8", {"start": v(-25.58, -2.82) * mm, "mid": v(-26.13, -3.18) * mm, "end": v(-26.64, -3.6) * mm});
            skArc(sketch, "E56.8.9", {"start": v(-24.95, -2.62) * mm, "mid": v(-25.28, -2.69) * mm, "end": v(-25.58, -2.82) * mm});
            skLineSegment(sketch, "E56.8.10", {"start": v(-24.95, -2.62) * mm, "end": v(-24.35, -2.55) * mm});
            skArc(sketch, "E56.8.11", {"start": v(-24.35, -2.55) * mm, "mid": v(-23.83, -2.27) * mm, "end": v(-23.65, -1.7) * mm});
            skArc(sketch, "E56.9.0", {"start": v(-21.33, -10.34) * mm, "mid": v(-21.77, -9.94) * mm, "end": v(-22.37, -9.97) * mm});
            skLineSegment(sketch, "E56.9.1", {"start": v(-22.91, -10.2) * mm, "end": v(-22.37, -9.97) * mm});
            skArc(sketch, "E56.9.2", {"start": v(-23.57, -10.34) * mm, "mid": v(-23.23, -10.31) * mm, "end": v(-22.91, -10.2) * mm});
            skArc(sketch, "E56.9.3", {"start": v(-23.57, -10.34) * mm, "mid": v(-24.22, -10.3) * mm, "end": v(-24.87, -10.2) * mm});
            skArc(sketch, "E56.9.4", {"start": v(-25.23, -9.91) * mm, "mid": v(-25.08, -10.1) * mm, "end": v(-24.87, -10.2) * mm});
            skLineSegment(sketch, "E56.9.5", {"start": v(-25.23, -9.91) * mm, "end": v(-25.31, -9.72) * mm});
            skLineSegment(sketch, "E56.9.6", {"start": v(-25.38, -9.51) * mm, "end": v(-25.31, -9.72) * mm});
            skArc(sketch, "E56.9.7", {"start": v(-25.3, -9.06) * mm, "mid": v(-25.4, -9.28) * mm, "end": v(-25.38, -9.51) * mm});
            skArc(sketch, "E56.9.8", {"start": v(-24.44, -8.08) * mm, "mid": v(-24.9, -8.55) * mm, "end": v(-25.3, -9.06) * mm});
            skArc(sketch, "E56.9.9", {"start": v(-23.86, -7.75) * mm, "mid": v(-24.16, -7.88) * mm, "end": v(-24.44, -8.08) * mm});
            skLineSegment(sketch, "E56.9.10", {"start": v(-23.86, -7.75) * mm, "end": v(-23.3, -7.56) * mm});
            skArc(sketch, "E56.9.11", {"start": v(-23.3, -7.56) * mm, "mid": v(-22.83, -7.18) * mm, "end": v(-22.77, -6.59) * mm});
            skArc(sketch, "E56.10.0", {"start": v(-18.71, -14.55) * mm, "mid": v(-19.23, -14.25) * mm, "end": v(-19.8, -14.4) * mm});
            skLineSegment(sketch, "E56.10.1", {"start": v(-20.29, -14.75) * mm, "end": v(-19.8, -14.4) * mm});
            skArc(sketch, "E56.10.2", {"start": v(-20.9, -15.02) * mm, "mid": v(-20.58, -14.92) * mm, "end": v(-20.29, -14.75) * mm});
            skArc(sketch, "E56.10.3", {"start": v(-20.9, -15.02) * mm, "mid": v(-21.55, -15.12) * mm, "end": v(-22.2, -15.15) * mm});
            skArc(sketch, "E56.10.4", {"start": v(-22.61, -14.94) * mm, "mid": v(-22.43, -15.1) * mm, "end": v(-22.2, -15.15) * mm});
            skLineSegment(sketch, "E56.10.5", {"start": v(-22.61, -14.94) * mm, "end": v(-22.74, -14.77) * mm});
            skLineSegment(sketch, "E56.10.6", {"start": v(-22.85, -14.58) * mm, "end": v(-22.74, -14.77) * mm});
            skArc(sketch, "E56.10.7", {"start": v(-22.87, -14.12) * mm, "mid": v(-22.91, -14.35) * mm, "end": v(-22.85, -14.58) * mm});
            skArc(sketch, "E56.10.8", {"start": v(-22.22, -12.99) * mm, "mid": v(-22.58, -13.54) * mm, "end": v(-22.87, -14.12) * mm});
            skArc(sketch, "E56.10.9", {"start": v(-21.73, -12.54) * mm, "mid": v(-22, -12.73) * mm, "end": v(-22.22, -12.99) * mm});
            skLineSegment(sketch, "E56.10.10", {"start": v(-21.73, -12.54) * mm, "end": v(-21.2, -12.24) * mm});
            skArc(sketch, "E56.10.11", {"start": v(-21.2, -12.24) * mm, "mid": v(-20.84, -11.77) * mm, "end": v(-20.9, -11.18) * mm});
            skArc(sketch, "E56.11.0", {"start": v(-15.28, -18.13) * mm, "mid": v(-15.85, -17.94) * mm, "end": v(-16.38, -18.2) * mm});
            skLineSegment(sketch, "E56.11.1", {"start": v(-16.78, -18.64) * mm, "end": v(-16.38, -18.2) * mm});
            skArc(sketch, "E56.11.2", {"start": v(-17.32, -19.04) * mm, "mid": v(-17.03, -18.87) * mm, "end": v(-16.78, -18.64) * mm});
            skArc(sketch, "E56.11.3", {"start": v(-17.32, -19.04) * mm, "mid": v(-17.94, -19.27) * mm, "end": v(-18.57, -19.44) * mm});
            skArc(sketch, "E56.11.4", {"start": v(-19.01, -19.32) * mm, "mid": v(-18.8, -19.43) * mm, "end": v(-18.57, -19.44) * mm});
            skLineSegment(sketch, "E56.11.5", {"start": v(-19.01, -19.32) * mm, "end": v(-19.17, -19.17) * mm});
            skLineSegment(sketch, "E56.11.6", {"start": v(-19.32, -19.01) * mm, "end": v(-19.17, -19.17) * mm});
            skArc(sketch, "E56.11.7", {"start": v(-19.44, -18.57) * mm, "mid": v(-19.43, -18.8) * mm, "end": v(-19.32, -19.01) * mm});
            skArc(sketch, "E56.11.8", {"start": v(-19.04, -17.32) * mm, "mid": v(-19.27, -17.94) * mm, "end": v(-19.44, -18.57) * mm});
            skArc(sketch, "E56.11.9", {"start": v(-18.64, -16.78) * mm, "mid": v(-18.87, -17.03) * mm, "end": v(-19.04, -17.32) * mm});
            skLineSegment(sketch, "E56.11.10", {"start": v(-18.64, -16.78) * mm, "end": v(-18.2, -16.38) * mm});
            skArc(sketch, "E56.11.11", {"start": v(-18.2, -16.38) * mm, "mid": v(-17.94, -15.85) * mm, "end": v(-18.13, -15.28) * mm});
            skArc(sketch, "E56.12.0", {"start": v(-11.18, -20.9) * mm, "mid": v(-11.77, -20.84) * mm, "end": v(-12.24, -21.2) * mm});
            skLineSegment(sketch, "E56.12.1", {"start": v(-12.54, -21.73) * mm, "end": v(-12.24, -21.2) * mm});
            skArc(sketch, "E56.12.2", {"start": v(-12.99, -22.22) * mm, "mid": v(-12.73, -22) * mm, "end": v(-12.54, -21.73) * mm});
            skArc(sketch, "E56.12.3", {"start": v(-12.99, -22.22) * mm, "mid": v(-13.54, -22.58) * mm, "end": v(-14.12, -22.87) * mm});
            skArc(sketch, "E56.12.4", {"start": v(-14.58, -22.85) * mm, "mid": v(-14.35, -22.91) * mm, "end": v(-14.12, -22.87) * mm});
            skLineSegment(sketch, "E56.12.5", {"start": v(-14.58, -22.85) * mm, "end": v(-14.77, -22.74) * mm});
            skLineSegment(sketch, "E56.12.6", {"start": v(-14.94, -22.61) * mm, "end": v(-14.77, -22.74) * mm});
            skArc(sketch, "E56.12.7", {"start": v(-15.15, -22.2) * mm, "mid": v(-15.1, -22.43) * mm, "end": v(-14.94, -22.61) * mm});
            skArc(sketch, "E56.12.8", {"start": v(-15.02, -20.9) * mm, "mid": v(-15.12, -21.55) * mm, "end": v(-15.15, -22.2) * mm});
            skArc(sketch, "E56.12.9", {"start": v(-14.75, -20.29) * mm, "mid": v(-14.92, -20.58) * mm, "end": v(-15.02, -20.9) * mm});
            skLineSegment(sketch, "E56.12.10", {"start": v(-14.75, -20.29) * mm, "end": v(-14.4, -19.8) * mm});
            skArc(sketch, "E56.12.11", {"start": v(-14.4, -19.8) * mm, "mid": v(-14.25, -19.23) * mm, "end": v(-14.55, -18.71) * mm});
            skArc(sketch, "E56.13.0", {"start": v(-6.59, -22.77) * mm, "mid": v(-7.18, -22.83) * mm, "end": v(-7.56, -23.3) * mm});
            skLineSegment(sketch, "E56.13.1", {"start": v(-7.75, -23.86) * mm, "end": v(-7.56, -23.3) * mm});
            skArc(sketch, "E56.13.2", {"start": v(-8.08, -24.44) * mm, "mid": v(-7.88, -24.16) * mm, "end": v(-7.75, -23.86) * mm});
            skArc(sketch, "E56.13.3", {"start": v(-8.08, -24.44) * mm, "mid": v(-8.55, -24.9) * mm, "end": v(-9.06, -25.3) * mm});
            skArc(sketch, "E56.13.4", {"start": v(-9.51, -25.38) * mm, "mid": v(-9.28, -25.4) * mm, "end": v(-9.06, -25.3) * mm});
            skLineSegment(sketch, "E56.13.5", {"start": v(-9.51, -25.38) * mm, "end": v(-9.72, -25.31) * mm});
            skLineSegment(sketch, "E56.13.6", {"start": v(-9.91, -25.23) * mm, "end": v(-9.72, -25.31) * mm});
            skArc(sketch, "E56.13.7", {"start": v(-10.2, -24.87) * mm, "mid": v(-10.1, -25.08) * mm, "end": v(-9.91, -25.23) * mm});
            skArc(sketch, "E56.13.8", {"start": v(-10.34, -23.57) * mm, "mid": v(-10.3, -24.22) * mm, "end": v(-10.2, -24.87) * mm});
            skArc(sketch, "E56.13.9", {"start": v(-10.2, -22.91) * mm, "mid": v(-10.31, -23.23) * mm, "end": v(-10.34, -23.57) * mm});
            skLineSegment(sketch, "E56.13.10", {"start": v(-10.2, -22.91) * mm, "end": v(-9.97, -22.37) * mm});
            skArc(sketch, "E56.13.11", {"start": v(-9.97, -22.37) * mm, "mid": v(-9.94, -21.77) * mm, "end": v(-10.34, -21.33) * mm});
            skArc(sketch, "E56.14.0", {"start": v(-1.7, -23.65) * mm, "mid": v(-2.27, -23.83) * mm, "end": v(-2.55, -24.35) * mm});
            skLineSegment(sketch, "E56.14.1", {"start": v(-2.62, -24.95) * mm, "end": v(-2.55, -24.35) * mm});
            skArc(sketch, "E56.14.2", {"start": v(-2.82, -25.58) * mm, "mid": v(-2.69, -25.28) * mm, "end": v(-2.62, -24.95) * mm});
            skArc(sketch, "E56.14.3", {"start": v(-2.82, -25.58) * mm, "mid": v(-3.18, -26.13) * mm, "end": v(-3.6, -26.64) * mm});
            skArc(sketch, "E56.14.4", {"start": v(-4.03, -26.8) * mm, "mid": v(-3.8, -26.77) * mm, "end": v(-3.6, -26.64) * mm});
            skLineSegment(sketch, "E56.14.5", {"start": v(-4.03, -26.8) * mm, "end": v(-4.24, -26.78) * mm});
            skLineSegment(sketch, "E56.14.6", {"start": v(-4.45, -26.74) * mm, "end": v(-4.24, -26.78) * mm});
            skArc(sketch, "E56.14.7", {"start": v(-4.8, -26.45) * mm, "mid": v(-4.66, -26.63) * mm, "end": v(-4.45, -26.74) * mm});
            skArc(sketch, "E56.14.8", {"start": v(-5.22, -25.2) * mm, "mid": v(-5.05, -25.84) * mm, "end": v(-4.8, -26.45) * mm});
            skArc(sketch, "E56.14.9", {"start": v(-5.22, -24.53) * mm, "mid": v(-5.26, -24.87) * mm, "end": v(-5.22, -25.2) * mm});
            skLineSegment(sketch, "E56.14.10", {"start": v(-5.22, -24.53) * mm, "end": v(-5.1, -23.95) * mm});
            skArc(sketch, "E56.14.11", {"start": v(-5.1, -23.95) * mm, "mid": v(-5.2, -23.36) * mm, "end": v(-5.68, -23.02) * mm});
            skArc(sketch, "E56.15.0", {"start": v(3.25, -23.48) * mm, "mid": v(2.73, -23.78) * mm, "end": v(2.57, -24.35) * mm});
            skLineSegment(sketch, "E56.15.1", {"start": v(2.63, -24.95) * mm, "end": v(2.57, -24.35) * mm});
            skArc(sketch, "E56.15.2", {"start": v(2.56, -25.61) * mm, "mid": v(2.63, -25.28) * mm, "end": v(2.63, -24.95) * mm});
            skArc(sketch, "E56.15.3", {"start": v(2.56, -25.61) * mm, "mid": v(2.32, -26.22) * mm, "end": v(2.02, -26.8) * mm});
            skArc(sketch, "E56.15.4", {"start": v(1.63, -27.05) * mm, "mid": v(1.86, -26.98) * mm, "end": v(2.02, -26.8) * mm});
            skLineSegment(sketch, "E56.15.5", {"start": v(1.63, -27.05) * mm, "end": v(1.42, -27.08) * mm});
            skLineSegment(sketch, "E56.15.6", {"start": v(1.2, -27.08) * mm, "end": v(1.42, -27.08) * mm});
            skArc(sketch, "E56.15.7", {"start": v(0.8, -26.87) * mm, "mid": v(0.97, -27.02) * mm, "end": v(1.2, -27.08) * mm});
            skArc(sketch, "E56.15.8", {"start": v(0.14, -25.74) * mm, "mid": v(0.44, -26.32) * mm, "end": v(0.8, -26.87) * mm});
            skArc(sketch, "E56.15.9", {"start": v(0, -25.08) * mm, "mid": v(0.03, -25.42) * mm, "end": v(0.14, -25.74) * mm});
            skLineSegment(sketch, "E56.15.10", {"start": v(0, -25.08) * mm, "end": v(0, -24.49) * mm});
            skArc(sketch, "E56.15.11", {"start": v(0, -24.49) * mm, "mid": v(-0.23, -23.94) * mm, "end": v(-0.77, -23.7) * mm});
            skArc(sketch, "E56.16.0", {"start": v(8.06, -22.3) * mm, "mid": v(7.61, -22.7) * mm, "end": v(7.57, -23.29) * mm});
            skLineSegment(sketch, "E56.16.1", {"start": v(7.76, -23.85) * mm, "end": v(7.57, -23.29) * mm});
            skArc(sketch, "E56.16.2", {"start": v(7.82, -24.52) * mm, "mid": v(7.83, -24.18) * mm, "end": v(7.76, -23.85) * mm});
            skArc(sketch, "E56.16.3", {"start": v(7.82, -24.52) * mm, "mid": v(7.72, -25.17) * mm, "end": v(7.55, -25.8) * mm});
            skArc(sketch, "E56.16.4", {"start": v(7.22, -26.12) * mm, "mid": v(7.42, -26) * mm, "end": v(7.55, -25.8) * mm});
            skLineSegment(sketch, "E56.16.5", {"start": v(7.22, -26.12) * mm, "end": v(7.02, -26.19) * mm});
            skLineSegment(sketch, "E56.16.6", {"start": v(6.8, -26.23) * mm, "end": v(7.02, -26.19) * mm});
            skArc(sketch, "E56.16.7", {"start": v(6.36, -26.12) * mm, "mid": v(6.57, -26.23) * mm, "end": v(6.8, -26.23) * mm});
            skArc(sketch, "E56.16.8", {"start": v(5.48, -25.15) * mm, "mid": v(5.9, -25.65) * mm, "end": v(6.36, -26.12) * mm});
            skArc(sketch, "E56.16.9", {"start": v(5.2, -24.54) * mm, "mid": v(5.31, -24.86) * mm, "end": v(5.48, -25.15) * mm});
            skLineSegment(sketch, "E56.16.10", {"start": v(5.2, -24.54) * mm, "end": v(5.09, -23.95) * mm});
            skArc(sketch, "E56.16.11", {"start": v(5.09, -23.95) * mm, "mid": v(4.75, -23.46) * mm, "end": v(4.17, -23.34) * mm});
            skArc(sketch, "E56.17.0", {"start": v(12.52, -20.13) * mm, "mid": v(12.17, -20.61) * mm, "end": v(12.25, -21.2) * mm});
            skLineSegment(sketch, "E56.17.1", {"start": v(12.55, -21.72) * mm, "end": v(12.25, -21.2) * mm});
            skArc(sketch, "E56.17.2", {"start": v(12.75, -22.36) * mm, "mid": v(12.68, -22.03) * mm, "end": v(12.55, -21.72) * mm});
            skArc(sketch, "E56.17.3", {"start": v(12.75, -22.36) * mm, "mid": v(12.78, -23.01) * mm, "end": v(12.75, -23.67) * mm});
            skArc(sketch, "E56.17.4", {"start": v(12.5, -24.05) * mm, "mid": v(12.67, -23.89) * mm, "end": v(12.75, -23.67) * mm});
            skLineSegment(sketch, "E56.17.5", {"start": v(12.5, -24.05) * mm, "end": v(12.3, -24.16) * mm});
            skLineSegment(sketch, "E56.17.6", {"start": v(12.11, -24.25) * mm, "end": v(12.3, -24.16) * mm});
            skArc(sketch, "E56.17.7", {"start": v(11.65, -24.22) * mm, "mid": v(11.88, -24.29) * mm, "end": v(12.11, -24.25) * mm});
            skArc(sketch, "E56.17.8", {"start": v(10.6, -23.46) * mm, "mid": v(11.1, -23.87) * mm, "end": v(11.65, -24.22) * mm});
            skArc(sketch, "E56.17.9", {"start": v(10.2, -22.92) * mm, "mid": v(10.37, -23.2) * mm, "end": v(10.6, -23.46) * mm});
            skLineSegment(sketch, "E56.17.10", {"start": v(10.2, -22.92) * mm, "end": v(9.95, -22.37) * mm});
            skArc(sketch, "E56.17.11", {"start": v(9.95, -22.37) * mm, "mid": v(9.53, -21.96) * mm, "end": v(8.93, -21.96) * mm});
            skArc(sketch, "E56.18.0", {"start": v(16.43, -17.1) * mm, "mid": v(16.19, -17.63) * mm, "end": v(16.39, -18.2) * mm});
            skLineSegment(sketch, "E56.18.1", {"start": v(16.79, -18.64) * mm, "end": v(16.39, -18.2) * mm});
            skArc(sketch, "E56.18.2", {"start": v(17.12, -19.22) * mm, "mid": v(16.99, -18.9) * mm, "end": v(16.79, -18.64) * mm});
            skArc(sketch, "E56.18.3", {"start": v(17.12, -19.22) * mm, "mid": v(17.29, -19.85) * mm, "end": v(17.39, -20.5) * mm});
            skArc(sketch, "E56.18.4", {"start": v(17.22, -20.93) * mm, "mid": v(17.36, -20.73) * mm, "end": v(17.39, -20.5) * mm});
            skLineSegment(sketch, "E56.18.5", {"start": v(17.22, -20.93) * mm, "end": v(17.06, -21.07) * mm});
            skLineSegment(sketch, "E56.18.6", {"start": v(16.89, -21.2) * mm, "end": v(17.06, -21.07) * mm});
            skArc(sketch, "E56.18.7", {"start": v(16.44, -21.27) * mm, "mid": v(16.67, -21.29) * mm, "end": v(16.89, -21.2) * mm});
            skArc(sketch, "E56.18.8", {"start": v(15.24, -20.74) * mm, "mid": v(15.82, -21.04) * mm, "end": v(16.44, -21.27) * mm});
            skArc(sketch, "E56.18.9", {"start": v(14.74, -20.3) * mm, "mid": v(14.96, -20.55) * mm, "end": v(15.24, -20.74) * mm});
            skLineSegment(sketch, "E56.18.10", {"start": v(14.74, -20.3) * mm, "end": v(14.39, -19.81) * mm});
            skArc(sketch, "E56.18.11", {"start": v(14.39, -19.81) * mm, "mid": v(13.88, -19.5) * mm, "end": v(13.3, -19.62) * mm});
            skArc(sketch, "E56.19.0", {"start": v(19.62, -13.3) * mm, "mid": v(19.5, -13.88) * mm, "end": v(19.81, -14.39) * mm});
            skLineSegment(sketch, "E56.19.1", {"start": v(20.3, -14.74) * mm, "end": v(19.81, -14.39) * mm});
            skArc(sketch, "E56.19.2", {"start": v(20.74, -15.24) * mm, "mid": v(20.55, -14.96) * mm, "end": v(20.3, -14.74) * mm});
            skArc(sketch, "E56.19.3", {"start": v(20.74, -15.24) * mm, "mid": v(21.04, -15.82) * mm, "end": v(21.27, -16.44) * mm});
            skArc(sketch, "E56.19.4", {"start": v(21.2, -16.89) * mm, "mid": v(21.29, -16.67) * mm, "end": v(21.27, -16.44) * mm});
            skLineSegment(sketch, "E56.19.5", {"start": v(21.2, -16.89) * mm, "end": v(21.07, -17.06) * mm});
            skLineSegment(sketch, "E56.19.6", {"start": v(20.93, -17.22) * mm, "end": v(21.07, -17.06) * mm});
            skArc(sketch, "E56.19.7", {"start": v(20.5, -17.39) * mm, "mid": v(20.73, -17.36) * mm, "end": v(20.93, -17.22) * mm});
            skArc(sketch, "E56.19.8", {"start": v(19.22, -17.12) * mm, "mid": v(19.85, -17.29) * mm, "end": v(20.5, -17.39) * mm});
            skArc(sketch, "E56.19.9", {"start": v(18.64, -16.79) * mm, "mid": v(18.9, -16.99) * mm, "end": v(19.22, -17.12) * mm});
            skLineSegment(sketch, "E56.19.10", {"start": v(18.64, -16.79) * mm, "end": v(18.2, -16.39) * mm});
            skArc(sketch, "E56.19.11", {"start": v(18.2, -16.39) * mm, "mid": v(17.63, -16.19) * mm, "end": v(17.1, -16.43) * mm});
            skArc(sketch, "E56.20.0", {"start": v(21.96, -8.93) * mm, "mid": v(21.96, -9.53) * mm, "end": v(22.37, -9.95) * mm});
            skLineSegment(sketch, "E56.20.1", {"start": v(22.92, -10.2) * mm, "end": v(22.37, -9.95) * mm});
            skArc(sketch, "E56.20.2", {"start": v(23.46, -10.6) * mm, "mid": v(23.2, -10.37) * mm, "end": v(22.92, -10.2) * mm});
            skArc(sketch, "E56.20.3", {"start": v(23.46, -10.6) * mm, "mid": v(23.87, -11.1) * mm, "end": v(24.22, -11.65) * mm});
            skArc(sketch, "E56.20.4", {"start": v(24.25, -12.11) * mm, "mid": v(24.29, -11.88) * mm, "end": v(24.22, -11.65) * mm});
            skLineSegment(sketch, "E56.20.5", {"start": v(24.25, -12.11) * mm, "end": v(24.16, -12.3) * mm});
            skLineSegment(sketch, "E56.20.6", {"start": v(24.05, -12.5) * mm, "end": v(24.16, -12.3) * mm});
            skArc(sketch, "E56.20.7", {"start": v(23.67, -12.75) * mm, "mid": v(23.89, -12.67) * mm, "end": v(24.05, -12.5) * mm});
            skArc(sketch, "E56.20.8", {"start": v(22.36, -12.75) * mm, "mid": v(23.01, -12.78) * mm, "end": v(23.67, -12.75) * mm});
            skArc(sketch, "E56.20.9", {"start": v(21.72, -12.55) * mm, "mid": v(22.03, -12.68) * mm, "end": v(22.36, -12.75) * mm});
            skLineSegment(sketch, "E56.20.10", {"start": v(21.72, -12.55) * mm, "end": v(21.2, -12.25) * mm});
            skArc(sketch, "E56.20.11", {"start": v(21.2, -12.25) * mm, "mid": v(20.61, -12.17) * mm, "end": v(20.13, -12.52) * mm});
            skArc(sketch, "E56.21.0", {"start": v(23.34, -4.17) * mm, "mid": v(23.46, -4.75) * mm, "end": v(23.95, -5.09) * mm});
            skLineSegment(sketch, "E56.21.1", {"start": v(24.54, -5.2) * mm, "end": v(23.95, -5.09) * mm});
            skArc(sketch, "E56.21.2", {"start": v(25.15, -5.48) * mm, "mid": v(24.86, -5.31) * mm, "end": v(24.54, -5.2) * mm});
            skArc(sketch, "E56.21.3", {"start": v(25.15, -5.48) * mm, "mid": v(25.65, -5.9) * mm, "end": v(26.12, -6.36) * mm});
            skArc(sketch, "E56.21.4", {"start": v(26.23, -6.8) * mm, "mid": v(26.23, -6.57) * mm, "end": v(26.12, -6.36) * mm});
            skLineSegment(sketch, "E56.21.5", {"start": v(26.23, -6.8) * mm, "end": v(26.19, -7.02) * mm});
            skLineSegment(sketch, "E56.21.6", {"start": v(26.12, -7.22) * mm, "end": v(26.19, -7.02) * mm});
            skArc(sketch, "E56.21.7", {"start": v(25.8, -7.55) * mm, "mid": v(26, -7.42) * mm, "end": v(26.12, -7.22) * mm});
            skArc(sketch, "E56.21.8", {"start": v(24.52, -7.82) * mm, "mid": v(25.17, -7.72) * mm, "end": v(25.8, -7.55) * mm});
            skArc(sketch, "E56.21.9", {"start": v(23.85, -7.76) * mm, "mid": v(24.18, -7.83) * mm, "end": v(24.52, -7.82) * mm});
            skLineSegment(sketch, "E56.21.10", {"start": v(23.85, -7.76) * mm, "end": v(23.29, -7.57) * mm});
            skArc(sketch, "E56.21.11", {"start": v(23.29, -7.57) * mm, "mid": v(22.7, -7.61) * mm, "end": v(22.3, -8.06) * mm});
            skArc(sketch, "E56.22.0", {"start": v(23.7, 0.77) * mm, "mid": v(23.94, 0.23) * mm, "end": v(24.49, 0) * mm});
            skLineSegment(sketch, "E56.22.1", {"start": v(25.08, 0) * mm, "end": v(24.49, 0) * mm});
            skArc(sketch, "E56.22.2", {"start": v(25.74, -0.14) * mm, "mid": v(25.42, -0.03) * mm, "end": v(25.08, 0) * mm});
            skArc(sketch, "E56.22.3", {"start": v(25.74, -0.14) * mm, "mid": v(26.32, -0.44) * mm, "end": v(26.87, -0.8) * mm});
            skArc(sketch, "E56.22.4", {"start": v(27.08, -1.2) * mm, "mid": v(27.02, -0.97) * mm, "end": v(26.87, -0.8) * mm});
            skLineSegment(sketch, "E56.22.5", {"start": v(27.08, -1.2) * mm, "end": v(27.08, -1.42) * mm});
            skLineSegment(sketch, "E56.22.6", {"start": v(27.05, -1.63) * mm, "end": v(27.08, -1.42) * mm});
            skArc(sketch, "E56.22.7", {"start": v(26.8, -2.02) * mm, "mid": v(26.98, -1.86) * mm, "end": v(27.05, -1.63) * mm});
            skArc(sketch, "E56.22.8", {"start": v(25.61, -2.56) * mm, "mid": v(26.22, -2.32) * mm, "end": v(26.8, -2.02) * mm});
            skArc(sketch, "E56.22.9", {"start": v(24.95, -2.63) * mm, "mid": v(25.28, -2.63) * mm, "end": v(25.61, -2.56) * mm});
            skLineSegment(sketch, "E56.22.10", {"start": v(24.95, -2.63) * mm, "end": v(24.35, -2.57) * mm});
            skArc(sketch, "E56.22.11", {"start": v(24.35, -2.57) * mm, "mid": v(23.78, -2.73) * mm, "end": v(23.48, -3.25) * mm});
            skArc(sketch, "E56.23.0", {"start": v(23.02, 5.68) * mm, "mid": v(23.36, 5.2) * mm, "end": v(23.95, 5.1) * mm});
            skLineSegment(sketch, "E56.23.1", {"start": v(24.53, 5.22) * mm, "end": v(23.95, 5.1) * mm});
            skArc(sketch, "E56.23.2", {"start": v(25.2, 5.22) * mm, "mid": v(24.87, 5.26) * mm, "end": v(24.53, 5.22) * mm});
            skArc(sketch, "E56.23.3", {"start": v(25.2, 5.22) * mm, "mid": v(25.84, 5.05) * mm, "end": v(26.45, 4.8) * mm});
            skArc(sketch, "E56.23.4", {"start": v(26.74, 4.45) * mm, "mid": v(26.63, 4.66) * mm, "end": v(26.45, 4.8) * mm});
            skLineSegment(sketch, "E56.23.5", {"start": v(26.74, 4.45) * mm, "end": v(26.78, 4.24) * mm});
            skLineSegment(sketch, "E56.23.6", {"start": v(26.8, 4.03) * mm, "end": v(26.78, 4.24) * mm});
            skArc(sketch, "E56.23.7", {"start": v(26.64, 3.6) * mm, "mid": v(26.77, 3.8) * mm, "end": v(26.8, 4.03) * mm});
            skArc(sketch, "E56.23.8", {"start": v(25.58, 2.82) * mm, "mid": v(26.13, 3.18) * mm, "end": v(26.64, 3.6) * mm});
            skArc(sketch, "E56.23.9", {"start": v(24.95, 2.62) * mm, "mid": v(25.28, 2.69) * mm, "end": v(25.58, 2.82) * mm});
            skLineSegment(sketch, "E56.23.10", {"start": v(24.95, 2.62) * mm, "end": v(24.35, 2.55) * mm});
            skArc(sketch, "E56.23.11", {"start": v(24.35, 2.55) * mm, "mid": v(23.83, 2.27) * mm, "end": v(23.65, 1.7) * mm});
            skArc(sketch, "E56.24.0", {"start": v(21.33, 10.34) * mm, "mid": v(21.77, 9.94) * mm, "end": v(22.37, 9.97) * mm});
            skLineSegment(sketch, "E56.24.1", {"start": v(22.91, 10.2) * mm, "end": v(22.37, 9.97) * mm});
            skArc(sketch, "E56.24.2", {"start": v(23.57, 10.34) * mm, "mid": v(23.23, 10.31) * mm, "end": v(22.91, 10.2) * mm});
            skArc(sketch, "E56.24.3", {"start": v(23.57, 10.34) * mm, "mid": v(24.22, 10.3) * mm, "end": v(24.87, 10.2) * mm});
            skArc(sketch, "E56.24.4", {"start": v(25.23, 9.91) * mm, "mid": v(25.08, 10.1) * mm, "end": v(24.87, 10.2) * mm});
            skLineSegment(sketch, "E56.24.5", {"start": v(25.23, 9.91) * mm, "end": v(25.31, 9.72) * mm});
            skLineSegment(sketch, "E56.24.6", {"start": v(25.38, 9.51) * mm, "end": v(25.31, 9.72) * mm});
            skArc(sketch, "E56.24.7", {"start": v(25.3, 9.06) * mm, "mid": v(25.4, 9.28) * mm, "end": v(25.38, 9.51) * mm});
            skArc(sketch, "E56.24.8", {"start": v(24.44, 8.08) * mm, "mid": v(24.9, 8.55) * mm, "end": v(25.3, 9.06) * mm});
            skArc(sketch, "E56.24.9", {"start": v(23.86, 7.75) * mm, "mid": v(24.16, 7.88) * mm, "end": v(24.44, 8.08) * mm});
            skLineSegment(sketch, "E56.24.10", {"start": v(23.86, 7.75) * mm, "end": v(23.3, 7.56) * mm});
            skArc(sketch, "E56.24.11", {"start": v(23.3, 7.56) * mm, "mid": v(22.83, 7.18) * mm, "end": v(22.77, 6.59) * mm});
            skArc(sketch, "E56.25.0", {"start": v(18.71, 14.55) * mm, "mid": v(19.23, 14.25) * mm, "end": v(19.8, 14.4) * mm});
            skLineSegment(sketch, "E56.25.1", {"start": v(20.29, 14.75) * mm, "end": v(19.8, 14.4) * mm});
            skArc(sketch, "E56.25.2", {"start": v(20.9, 15.02) * mm, "mid": v(20.58, 14.92) * mm, "end": v(20.29, 14.75) * mm});
            skArc(sketch, "E56.25.3", {"start": v(20.9, 15.02) * mm, "mid": v(21.55, 15.12) * mm, "end": v(22.2, 15.15) * mm});
            skArc(sketch, "E56.25.4", {"start": v(22.61, 14.94) * mm, "mid": v(22.43, 15.1) * mm, "end": v(22.2, 15.15) * mm});
            skLineSegment(sketch, "E56.25.5", {"start": v(22.61, 14.94) * mm, "end": v(22.74, 14.77) * mm});
            skLineSegment(sketch, "E56.25.6", {"start": v(22.85, 14.58) * mm, "end": v(22.74, 14.77) * mm});
            skArc(sketch, "E56.25.7", {"start": v(22.87, 14.12) * mm, "mid": v(22.91, 14.35) * mm, "end": v(22.85, 14.58) * mm});
            skArc(sketch, "E56.25.8", {"start": v(22.22, 12.99) * mm, "mid": v(22.58, 13.54) * mm, "end": v(22.87, 14.12) * mm});
            skArc(sketch, "E56.25.9", {"start": v(21.73, 12.54) * mm, "mid": v(22, 12.73) * mm, "end": v(22.22, 12.99) * mm});
            skLineSegment(sketch, "E56.25.10", {"start": v(21.73, 12.54) * mm, "end": v(21.2, 12.24) * mm});
            skArc(sketch, "E56.25.11", {"start": v(21.2, 12.24) * mm, "mid": v(20.84, 11.77) * mm, "end": v(20.9, 11.18) * mm});
            skArc(sketch, "E56.26.0", {"start": v(15.28, 18.13) * mm, "mid": v(15.85, 17.94) * mm, "end": v(16.38, 18.2) * mm});
            skLineSegment(sketch, "E56.26.1", {"start": v(16.78, 18.64) * mm, "end": v(16.38, 18.2) * mm});
            skArc(sketch, "E56.26.2", {"start": v(17.32, 19.04) * mm, "mid": v(17.03, 18.87) * mm, "end": v(16.78, 18.64) * mm});
            skArc(sketch, "E56.26.3", {"start": v(17.32, 19.04) * mm, "mid": v(17.94, 19.27) * mm, "end": v(18.57, 19.44) * mm});
            skArc(sketch, "E56.26.4", {"start": v(19.01, 19.32) * mm, "mid": v(18.8, 19.43) * mm, "end": v(18.57, 19.44) * mm});
            skLineSegment(sketch, "E56.26.5", {"start": v(19.01, 19.32) * mm, "end": v(19.17, 19.17) * mm});
            skLineSegment(sketch, "E56.26.6", {"start": v(19.32, 19.01) * mm, "end": v(19.17, 19.17) * mm});
            skArc(sketch, "E56.26.7", {"start": v(19.44, 18.57) * mm, "mid": v(19.43, 18.8) * mm, "end": v(19.32, 19.01) * mm});
            skArc(sketch, "E56.26.8", {"start": v(19.04, 17.32) * mm, "mid": v(19.27, 17.94) * mm, "end": v(19.44, 18.57) * mm});
            skArc(sketch, "E56.26.9", {"start": v(18.64, 16.78) * mm, "mid": v(18.87, 17.03) * mm, "end": v(19.04, 17.32) * mm});
            skLineSegment(sketch, "E56.26.10", {"start": v(18.64, 16.78) * mm, "end": v(18.2, 16.38) * mm});
            skArc(sketch, "E56.26.11", {"start": v(18.2, 16.38) * mm, "mid": v(17.94, 15.85) * mm, "end": v(18.13, 15.28) * mm});
            skArc(sketch, "E56.27.0", {"start": v(11.18, 20.9) * mm, "mid": v(11.77, 20.84) * mm, "end": v(12.24, 21.2) * mm});
            skLineSegment(sketch, "E56.27.1", {"start": v(12.54, 21.73) * mm, "end": v(12.24, 21.2) * mm});
            skArc(sketch, "E56.27.2", {"start": v(12.99, 22.22) * mm, "mid": v(12.73, 22) * mm, "end": v(12.54, 21.73) * mm});
            skArc(sketch, "E56.27.3", {"start": v(12.99, 22.22) * mm, "mid": v(13.54, 22.58) * mm, "end": v(14.12, 22.87) * mm});
            skArc(sketch, "E56.27.4", {"start": v(14.58, 22.85) * mm, "mid": v(14.35, 22.91) * mm, "end": v(14.12, 22.87) * mm});
            skLineSegment(sketch, "E56.27.5", {"start": v(14.58, 22.85) * mm, "end": v(14.77, 22.74) * mm});
            skLineSegment(sketch, "E56.27.6", {"start": v(14.94, 22.61) * mm, "end": v(14.77, 22.74) * mm});
            skArc(sketch, "E56.27.7", {"start": v(15.15, 22.2) * mm, "mid": v(15.1, 22.43) * mm, "end": v(14.94, 22.61) * mm});
            skArc(sketch, "E56.27.8", {"start": v(15.02, 20.9) * mm, "mid": v(15.12, 21.55) * mm, "end": v(15.15, 22.2) * mm});
            skArc(sketch, "E56.27.9", {"start": v(14.75, 20.29) * mm, "mid": v(14.92, 20.58) * mm, "end": v(15.02, 20.9) * mm});
            skLineSegment(sketch, "E56.27.10", {"start": v(14.75, 20.29) * mm, "end": v(14.4, 19.8) * mm});
            skArc(sketch, "E56.27.11", {"start": v(14.4, 19.8) * mm, "mid": v(14.25, 19.23) * mm, "end": v(14.55, 18.71) * mm});
            skArc(sketch, "E56.28.0", {"start": v(6.59, 22.77) * mm, "mid": v(7.18, 22.83) * mm, "end": v(7.56, 23.3) * mm});
            skLineSegment(sketch, "E56.28.1", {"start": v(7.75, 23.86) * mm, "end": v(7.56, 23.3) * mm});
            skArc(sketch, "E56.28.2", {"start": v(8.08, 24.44) * mm, "mid": v(7.88, 24.16) * mm, "end": v(7.75, 23.86) * mm});
            skArc(sketch, "E56.28.3", {"start": v(8.08, 24.44) * mm, "mid": v(8.55, 24.9) * mm, "end": v(9.06, 25.3) * mm});
            skArc(sketch, "E56.28.4", {"start": v(9.51, 25.38) * mm, "mid": v(9.28, 25.4) * mm, "end": v(9.06, 25.3) * mm});
            skLineSegment(sketch, "E56.28.5", {"start": v(9.51, 25.38) * mm, "end": v(9.72, 25.31) * mm});
            skLineSegment(sketch, "E56.28.6", {"start": v(9.91, 25.23) * mm, "end": v(9.72, 25.31) * mm});
            skArc(sketch, "E56.28.7", {"start": v(10.2, 24.87) * mm, "mid": v(10.1, 25.08) * mm, "end": v(9.91, 25.23) * mm});
            skArc(sketch, "E56.28.8", {"start": v(10.34, 23.57) * mm, "mid": v(10.3, 24.22) * mm, "end": v(10.2, 24.87) * mm});
            skArc(sketch, "E56.28.9", {"start": v(10.2, 22.91) * mm, "mid": v(10.31, 23.23) * mm, "end": v(10.34, 23.57) * mm});
            skLineSegment(sketch, "E56.28.10", {"start": v(10.2, 22.91) * mm, "end": v(9.97, 22.37) * mm});
            skArc(sketch, "E56.28.11", {"start": v(9.97, 22.37) * mm, "mid": v(9.94, 21.77) * mm, "end": v(10.34, 21.33) * mm});
            skArc(sketch, "E56.29.0", {"start": v(1.7, 23.65) * mm, "mid": v(2.27, 23.83) * mm, "end": v(2.55, 24.35) * mm});
            skLineSegment(sketch, "E56.29.1", {"start": v(2.62, 24.95) * mm, "end": v(2.55, 24.35) * mm});
            skArc(sketch, "E56.29.2", {"start": v(2.82, 25.58) * mm, "mid": v(2.69, 25.28) * mm, "end": v(2.62, 24.95) * mm});
            skArc(sketch, "E56.29.3", {"start": v(2.82, 25.58) * mm, "mid": v(3.18, 26.13) * mm, "end": v(3.6, 26.64) * mm});
            skArc(sketch, "E56.29.4", {"start": v(4.03, 26.8) * mm, "mid": v(3.8, 26.77) * mm, "end": v(3.6, 26.64) * mm});
            skLineSegment(sketch, "E56.29.5", {"start": v(4.03, 26.8) * mm, "end": v(4.24, 26.78) * mm});
            skLineSegment(sketch, "E56.29.6", {"start": v(4.45, 26.74) * mm, "end": v(4.24, 26.78) * mm});
            skArc(sketch, "E56.29.7", {"start": v(4.8, 26.45) * mm, "mid": v(4.66, 26.63) * mm, "end": v(4.45, 26.74) * mm});
            skArc(sketch, "E56.29.8", {"start": v(5.22, 25.2) * mm, "mid": v(5.05, 25.84) * mm, "end": v(4.8, 26.45) * mm});
            skArc(sketch, "E56.29.9", {"start": v(5.22, 24.53) * mm, "mid": v(5.26, 24.87) * mm, "end": v(5.22, 25.2) * mm});
            skLineSegment(sketch, "E56.29.10", {"start": v(5.22, 24.53) * mm, "end": v(5.1, 23.95) * mm});
            skArc(sketch, "E56.29.11", {"start": v(5.1, 23.95) * mm, "mid": v(5.2, 23.36) * mm, "end": v(5.68, 23.02) * mm});
            skArc(sketch, "E57.trimOffspring", {"start": v(1.7, 23.65) * mm, "mid": v(1.24, 23.67) * mm, "end": v(0.77, 23.7) * mm});
            skArc(sketch, "E58.trimOffspring", {"start": v(6.59, 22.77) * mm, "mid": v(6.14, 22.9) * mm, "end": v(5.68, 23.02) * mm});
            skArc(sketch, "E59.trimOffspring", {"start": v(11.18, 20.9) * mm, "mid": v(10.76, 21.12) * mm, "end": v(10.34, 21.33) * mm});
            skArc(sketch, "E60.trimOffspring", {"start": v(15.28, 18.13) * mm, "mid": v(14.92, 18.42) * mm, "end": v(14.55, 18.71) * mm});
            skArc(sketch, "E61.trimOffspring", {"start": v(18.71, 14.55) * mm, "mid": v(18.42, 14.92) * mm, "end": v(18.13, 15.28) * mm});
            skArc(sketch, "E62.trimOffspring", {"start": v(21.33, 10.34) * mm, "mid": v(21.12, 10.76) * mm, "end": v(20.9, 11.18) * mm});
            skArc(sketch, "E63.trimOffspring", {"start": v(23.02, 5.68) * mm, "mid": v(22.9, 6.14) * mm, "end": v(22.77, 6.59) * mm});
            skArc(sketch, "E64.trimOffspring", {"start": v(23.7, 0.77) * mm, "mid": v(23.67, 1.24) * mm, "end": v(23.65, 1.7) * mm});
            skArc(sketch, "E65.trimOffspring", {"start": v(23.34, -4.17) * mm, "mid": v(23.41, -3.7) * mm, "end": v(23.48, -3.25) * mm});
            skArc(sketch, "E66.trimOffspring", {"start": v(21.96, -8.93) * mm, "mid": v(22.13, -8.5) * mm, "end": v(22.3, -8.06) * mm});
            skArc(sketch, "E67.trimOffspring", {"start": v(19.62, -13.3) * mm, "mid": v(19.88, -12.91) * mm, "end": v(20.13, -12.52) * mm});
            skArc(sketch, "E68.trimOffspring", {"start": v(16.43, -17.1) * mm, "mid": v(16.76, -16.76) * mm, "end": v(17.1, -16.43) * mm});
            skArc(sketch, "E69.trimOffspring", {"start": v(12.52, -20.13) * mm, "mid": v(12.91, -19.88) * mm, "end": v(13.3, -19.62) * mm});
            skArc(sketch, "E70.trimOffspring", {"start": v(8.06, -22.3) * mm, "mid": v(8.5, -22.13) * mm, "end": v(8.93, -21.96) * mm});
            skArc(sketch, "E71.trimOffspring", {"start": v(3.25, -23.48) * mm, "mid": v(3.7, -23.41) * mm, "end": v(4.17, -23.34) * mm});
            skArc(sketch, "E72.trimOffspring", {"start": v(-1.7, -23.65) * mm, "mid": v(-1.24, -23.67) * mm, "end": v(-0.77, -23.7) * mm});
            skArc(sketch, "E73.trimOffspring", {"start": v(-6.59, -22.77) * mm, "mid": v(-6.14, -22.9) * mm, "end": v(-5.68, -23.02) * mm});
            skArc(sketch, "E74.trimOffspring", {"start": v(-11.18, -20.9) * mm, "mid": v(-10.76, -21.12) * mm, "end": v(-10.34, -21.33) * mm});
            skArc(sketch, "E75.trimOffspring", {"start": v(-15.28, -18.13) * mm, "mid": v(-14.92, -18.42) * mm, "end": v(-14.55, -18.71) * mm});
            skArc(sketch, "E76.trimOffspring", {"start": v(-18.71, -14.55) * mm, "mid": v(-18.42, -14.92) * mm, "end": v(-18.13, -15.28) * mm});
            skArc(sketch, "E77.trimOffspring", {"start": v(-21.33, -10.34) * mm, "mid": v(-21.12, -10.76) * mm, "end": v(-20.9, -11.18) * mm});
            skArc(sketch, "E78.trimOffspring", {"start": v(-23.02, -5.68) * mm, "mid": v(-22.9, -6.14) * mm, "end": v(-22.77, -6.59) * mm});
            skArc(sketch, "E79.trimOffspring", {"start": v(-8.06, 22.3) * mm, "mid": v(-8.5, 22.13) * mm, "end": v(-8.93, 21.96) * mm});
            skArc(sketch, "E80.trimOffspring", {"start": v(-12.52, 20.13) * mm, "mid": v(-12.91, 19.88) * mm, "end": v(-13.3, 19.62) * mm});
            skArc(sketch, "E81.trimOffspring", {"start": v(-16.43, 17.1) * mm, "mid": v(-16.76, 16.76) * mm, "end": v(-17.1, 16.43) * mm});
            skArc(sketch, "E82.trimOffspring", {"start": v(-23.7, -0.77) * mm, "mid": v(-23.67, -1.24) * mm, "end": v(-23.65, -1.7) * mm});
            skArc(sketch, "E83.trimOffspring", {"start": v(-23.34, 4.17) * mm, "mid": v(-23.41, 3.7) * mm, "end": v(-23.48, 3.25) * mm});
            skArc(sketch, "E84.trimOffspring", {"start": v(-21.96, 8.93) * mm, "mid": v(-22.13, 8.5) * mm, "end": v(-22.3, 8.06) * mm});
            skArc(sketch, "E85.trimOffspring", {"start": v(-19.62, 13.3) * mm, "mid": v(-19.88, 12.91) * mm, "end": v(-20.13, 12.52) * mm});
            skSolve(sketch);
        }
        {
            var Q0;
            Q0=makeQuery(id+"F0.imprint","IMPRINT",FACE,{"disambiguationData":[TD([[makeQuery(id+"F0.imprint","IMPRINT",EDGE,{"derivedFrom":sQuery(id+"F0.wireOp",EDGE,"E0")}),1.0]])]});
            var Q1;
            Q1=makeQuery(id+"F2.imprint","IMPRINT",FACE,{"disambiguationData":[TD([[makeQuery(id+"F2.imprint","IMPRINT",EDGE,{"derivedFrom":sQuery(id+"F2.wireOp",EDGE,"E43")}),1.0]])]});
            var Q2;
            Q2=sQuery(id+"F0.wireOp",VERTEX,"E13.1.3.start");
            var Q3;
            Q3=sQuery(id+"F2.wireOp",VERTEX,"E56.29.3.start");
            loft(context, id + "F3", {"sheetProfilesArray" : [{ "sheetProfileEntities" : qUnion([Q0]) }, { "sheetProfileEntities" : qUnion([Q1]) }], "matchConnections" : true, "connections" : [{ "connectionEntities" : qUnion([Q2, Q3]), "connectionEdgeQueries" : qUnion([]), "connectionEdgeParameters" : [] }]});
        }
        {
            var Q0;
            Q0=makeQuery(id+"F3.opLoft","CAP_FACE",FACE,{"disambiguationData":[OSD([makeQuery(id+"F2.imprint","IMPRINT",FACE,{"disambiguationData":[TD([[makeQuery(id+"F2.imprint","IMPRINT",EDGE,{"derivedFrom":sQuery(id+"F2.wireOp",EDGE,"E43")}),1.0]])]})])],"isStart":true});
            var sketch = newSketch(context, id + "F4", { "sketchPlane" : qUnion([Q0])});
            skPoint(sketch, "E86", {"position": v(0, 0) * mm});
            skSolve(sketch);
        }
        {
            var Q0;
            Q0=sQuery(id+"F4.wireOp",VERTEX,"E86");
            var Q1;
            Q1=makeQuery(id+"F3.opLoft","SWEPT_BODY",BODY,{"disambiguationData":[OSD([makeQuery(id+"F0.imprint","IMPRINT",FACE,{"disambiguationData":[TD([[makeQuery(id+"F0.imprint","IMPRINT",EDGE,{"derivedFrom":sQuery(id+"F0.wireOp",EDGE,"E0")}),1.0]])]}),makeQuery(id+"F2.imprint","IMPRINT",FACE,{"disambiguationData":[TD([[makeQuery(id+"F2.imprint","IMPRINT",EDGE,{"derivedFrom":sQuery(id+"F2.wireOp",EDGE,"E43")}),1.0]])]})])]});
            hole(context, id + "F5", {"style" : HoleStyle.SIMPLE, "endStyle" : HoleEndStyle.THROUGH, "holeDiameter" : 12.7 * mm, "tappedDepth" : 12.7 * mm, "tapClearance" : 3, "locations" : qUnion([Q0]), "scope" : qUnion([Q1])});
        }
    });
